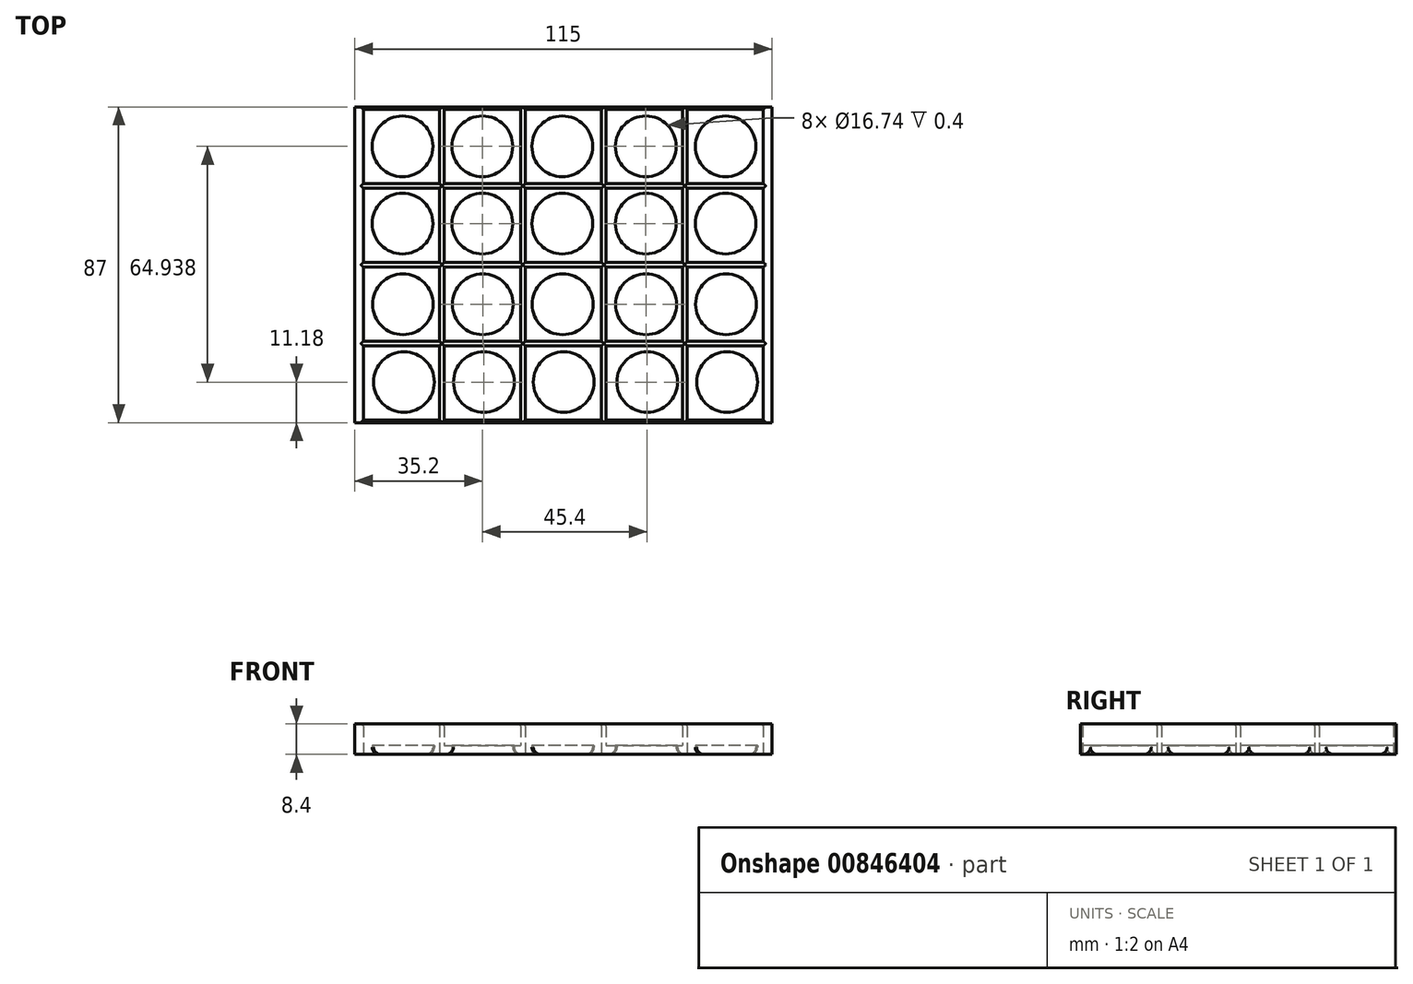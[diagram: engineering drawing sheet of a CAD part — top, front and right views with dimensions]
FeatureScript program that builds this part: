
annotation { "Feature Type Name" : "Feature", "Feature Type Description" : "" }
export const myFeature = defineFeature(function(context is Context, id is Id, definition is map)
    precondition{}
    {
        {
            var Q0;
            Q0=qCreatedBy(makeId("Top.planeOp"),FACE);
            var sketch = newSketch(context, id + "F0", { "sketchPlane" : qUnion([Q0])});
            skLineSegment(sketch, "E0.bottom", {"start": v(-57.5, 43.5) * mm, "end": v(57.5, 43.5) * mm});
            skLineSegment(sketch, "E0.top", {"start": v(-57.5, -43.5) * mm, "end": v(57.5, -43.5) * mm});
            skLineSegment(sketch, "E0.left", {"start": v(-57.5, 43.5) * mm, "end": v(-57.5, -43.5) * mm});
            skLineSegment(sketch, "E0.right", {"start": v(57.5, 43.5) * mm, "end": v(57.5, -43.5) * mm});
            skPoint(sketch, "E0.middle", {"position": v(0, 0) * mm});
            skCircle(sketch, "E1.MirrorC", {"center": v(-44.2, -10.9) * mm, "radius": 8.37 * mm});
            skCircle(sketch, "E2.MirrorC", {"center": v(-22.2, -10.9) * mm, "radius": 8.37 * mm});
            skCircle(sketch, "E3.MirrorC", {"center": v(-0.2, -10.9) * mm, "radius": 8.37 * mm});
            skCircle(sketch, "E4.MirrorC", {"center": v(22.8, -10.9) * mm, "radius": 8.37 * mm});
            skCircle(sketch, "E5.MirrorC", {"center": v(44.8, -10.9) * mm, "radius": 8.37 * mm});
            skLineSegment(sketch, "E6.0", {"start": v(-57.5, 42.8) * mm, "end": v(57.5, 42.8) * mm});
            skLineSegment(sketch, "E7.0", {"start": v(-57.5, -42.8) * mm, "end": v(57.5, -42.8) * mm});
            skLineSegment(sketch, "E8.0", {"start": v(-57.5, 22.32) * mm, "end": v(57.5, 22.32) * mm});
            skLineSegment(sketch, "E9.0", {"start": v(-57.5, -22.32) * mm, "end": v(57.5, -22.32) * mm});
            skLineSegment(sketch, "E10.0", {"start": v(-57.5, 21.12) * mm, "end": v(57.5, 21.12) * mm});
            skLineSegment(sketch, "E11.0", {"start": v(-57.5, -21.12) * mm, "end": v(57.5, -21.12) * mm});
            skLineSegment(sketch, "E12.0", {"start": v(-57.5, 0.64) * mm, "end": v(57.5, 0.64) * mm});
            skLineSegment(sketch, "E13.0", {"start": v(-57.5, -0.64) * mm, "end": v(57.5, -0.64) * mm});
            skLineSegment(sketch, "E14.0", {"start": v(55.1, 44.5) * mm, "end": v(55.1, -43.5) * mm});
            skLineSegment(sketch, "E15.0", {"start": v(34.1, 44.5) * mm, "end": v(34.1, -43.5) * mm});
            skLineSegment(sketch, "E16.0", {"start": v(32.8, 44.5) * mm, "end": v(32.8, -43.5) * mm});
            skLineSegment(sketch, "E17.0", {"start": v(11.8, 44.5) * mm, "end": v(11.8, -43.5) * mm});
            skLineSegment(sketch, "E18.0", {"start": v(10.5, 44.5) * mm, "end": v(10.5, -43.5) * mm});
            skLineSegment(sketch, "E19.0", {"start": v(-10.5, 44.5) * mm, "end": v(-10.5, -43.5) * mm});
            skLineSegment(sketch, "E20.0", {"start": v(-11.8, 44.5) * mm, "end": v(-11.8, -43.5) * mm});
            skLineSegment(sketch, "E21.0", {"start": v(-32.8, 44.5) * mm, "end": v(-32.8, -43.5) * mm});
            skLineSegment(sketch, "E22.0", {"start": v(-34.1, 44.5) * mm, "end": v(-34.1, -43.5) * mm});
            skLineSegment(sketch, "E23.0", {"start": v(-55.1, 44.5) * mm, "end": v(-55.1, -43.5) * mm});
            skCircle(sketch, "E24.MirrorC", {"center": v(-43.9, -32.32) * mm, "radius": 8.37 * mm});
            skCircle(sketch, "E25.MirrorC", {"center": v(-21.9, -32.32) * mm, "radius": 8.37 * mm});
            skCircle(sketch, "E26.MirrorC", {"center": v(0.1, -32.32) * mm, "radius": 8.37 * mm});
            skCircle(sketch, "E27.MirrorC", {"center": v(23.1, -32.32) * mm, "radius": 8.37 * mm});
            skCircle(sketch, "E28.MirrorC", {"center": v(45.1, -32.32) * mm, "radius": 8.37 * mm});
            skCircle(sketch, "E29.MirrorC", {"center": v(-44.3, 11.34) * mm, "radius": 8.37 * mm});
            skCircle(sketch, "E30.MirrorC", {"center": v(-22.3, 11.34) * mm, "radius": 8.37 * mm});
            skCircle(sketch, "E31.MirrorC", {"center": v(-0.3, 11.34) * mm, "radius": 8.37 * mm});
            skCircle(sketch, "E32.MirrorC", {"center": v(22.7, 11.34) * mm, "radius": 8.37 * mm});
            skCircle(sketch, "E33.MirrorC", {"center": v(44.7, 11.34) * mm, "radius": 8.37 * mm});
            skCircle(sketch, "E34.MirrorC", {"center": v(-44.3, 32.62) * mm, "radius": 8.37 * mm});
            skCircle(sketch, "E35.MirrorC", {"center": v(-22.3, 32.62) * mm, "radius": 8.37 * mm});
            skCircle(sketch, "E36.MirrorC", {"center": v(-0.3, 32.62) * mm, "radius": 8.37 * mm});
            skCircle(sketch, "E37.MirrorC", {"center": v(22.7, 32.62) * mm, "radius": 8.37 * mm});
            skCircle(sketch, "E38.MirrorC", {"center": v(44.7, 32.62) * mm, "radius": 8.37 * mm});
            skSolve(sketch);
        }
        {
            var Q0;
            {var subQ0=sQuery(id+"F0.wireOp",EDGE,"85c74178-88a3-4eaf-b492-32c6037f9e62.0");var subQ1=sQuery(id+"F0.wireOp",EDGE,"E0.left");var subQ2=makeQuery(id+"F0.imprint","INTERSECT",VERTEX,{"derivedFrom":[subQ1,subQ0]});Q0=makeQuery(id+"F0.imprint","IMPRINT",FACE,{"disambiguationData":[TD([[makeQuery(id+"F0.imprint","IMPRINT",EDGE,{"disambiguationData":[TD([[subQ2,-1.0]])],"derivedFrom":subQ1}),1.0]])]});}
            var Q1;
            {var subQ1=sQuery(id+"F0.wireOp",EDGE,"E0.bottom");var subQ6=sQuery(id+"F0.wireOp",EDGE,"E0.left");var subQ7=makeQuery(id+"F0.imprint","INTERSECT",VERTEX,{"derivedFrom":[subQ1,subQ6]});Q1=makeQuery(id+"F0.imprint","IMPRINT",FACE,{"disambiguationData":[TD([[makeQuery(id+"F0.imprint","IMPRINT",EDGE,{"disambiguationData":[TD([[subQ7,-1.0]])],"derivedFrom":subQ1}),-1.0]])]});}
            var Q2;
            {var subQ0=sQuery(id+"F0.wireOp",EDGE,"bdac1eed-a409-4cee-9b7b-61454a391d7d.0");var subQ1=sQuery(id+"F0.wireOp",EDGE,"E0.bottom");var subQ2=makeQuery(id+"F0.imprint","INTERSECT",VERTEX,{"derivedFrom":[subQ1,subQ0]});Q2=makeQuery(id+"F0.imprint","IMPRINT",FACE,{"disambiguationData":[TD([[makeQuery(id+"F0.imprint","IMPRINT",EDGE,{"disambiguationData":[TD([[subQ2,1.0]])],"derivedFrom":subQ1}),-1.0]])]});}
            var Q3;
            {var subQ0=sQuery(id+"F0.wireOp",EDGE,"23e37434-4ebb-4948-80c8-8d17bba51405.0");var subQ1=sQuery(id+"F0.wireOp",EDGE,"E0.bottom");var subQ2=makeQuery(id+"F0.imprint","INTERSECT",VERTEX,{"derivedFrom":[subQ1,subQ0]});Q3=makeQuery(id+"F0.imprint","IMPRINT",FACE,{"disambiguationData":[TD([[makeQuery(id+"F0.imprint","IMPRINT",EDGE,{"disambiguationData":[TD([[subQ2,1.0]])],"derivedFrom":subQ1}),-1.0]])]});}
            var Q4;
            {var subQ0=sQuery(id+"F0.wireOp",EDGE,"85c74178-88a3-4eaf-b492-32c6037f9e62.0");var subQ1=sQuery(id+"F0.wireOp",EDGE,"23e37434-4ebb-4948-80c8-8d17bba51405.0");var subQ2=makeQuery(id+"F0.imprint","INTERSECT",VERTEX,{"derivedFrom":[subQ1,subQ0]});Q4=makeQuery(id+"F0.imprint","IMPRINT",FACE,{"disambiguationData":[TD([[makeQuery(id+"F0.imprint","IMPRINT",EDGE,{"disambiguationData":[TD([[subQ2,-1.0]])],"derivedFrom":subQ1}),-1.0]])]});}
            var Q5;
            {var subQ0=sQuery(id+"F0.wireOp",EDGE,"f9003588-73a7-42be-b55c-edd191297de8.0");var subQ1=sQuery(id+"F0.wireOp",EDGE,"E0.bottom");var subQ2=makeQuery(id+"F0.imprint","INTERSECT",VERTEX,{"derivedFrom":[subQ1,subQ0]});Q5=makeQuery(id+"F0.imprint","IMPRINT",FACE,{"disambiguationData":[TD([[makeQuery(id+"F0.imprint","IMPRINT",EDGE,{"disambiguationData":[TD([[subQ2,1.0]])],"derivedFrom":subQ1}),-1.0]])]});}
            var Q6;
            {var subQ0=sQuery(id+"F0.wireOp",EDGE,"a62689d6-4df4-411d-a8de-d30e4e7abbb4.0");var subQ1=sQuery(id+"F0.wireOp",EDGE,"E0.bottom");var subQ2=makeQuery(id+"F0.imprint","INTERSECT",VERTEX,{"derivedFrom":[subQ1,subQ0]});Q6=makeQuery(id+"F0.imprint","IMPRINT",FACE,{"disambiguationData":[TD([[makeQuery(id+"F0.imprint","IMPRINT",EDGE,{"disambiguationData":[TD([[subQ2,1.0]])],"derivedFrom":subQ1}),-1.0]])]});}
            var Q7;
            {var subQ0=sQuery(id+"F0.wireOp",EDGE,"989afcd3-5a0d-4914-9734-28e95c678f40.0");var subQ1=sQuery(id+"F0.wireOp",EDGE,"E0.bottom");var subQ2=makeQuery(id+"F0.imprint","INTERSECT",VERTEX,{"derivedFrom":[subQ1,subQ0]});Q7=makeQuery(id+"F0.imprint","IMPRINT",FACE,{"disambiguationData":[TD([[makeQuery(id+"F0.imprint","IMPRINT",EDGE,{"disambiguationData":[TD([[subQ2,1.0]])],"derivedFrom":subQ1}),-1.0]])]});}
            var Q8;
            {var subQ0=sQuery(id+"F0.wireOp",EDGE,"862523a1-1db9-4ec9-a786-b55df2c1a98e.0");var subQ1=sQuery(id+"F0.wireOp",EDGE,"E0.bottom");var subQ2=makeQuery(id+"F0.imprint","INTERSECT",VERTEX,{"derivedFrom":[subQ1,subQ0]});Q8=makeQuery(id+"F0.imprint","IMPRINT",FACE,{"disambiguationData":[TD([[makeQuery(id+"F0.imprint","IMPRINT",EDGE,{"disambiguationData":[TD([[subQ2,1.0]])],"derivedFrom":subQ1}),-1.0]])]});}
            var Q9;
            {var subQ0=sQuery(id+"F0.wireOp",EDGE,"E0.right");var subQ1=sQuery(id+"F0.wireOp",EDGE,"E0.bottom");var subQ2=makeQuery(id+"F0.imprint","INTERSECT",VERTEX,{"derivedFrom":[subQ1,subQ0]});Q9=makeQuery(id+"F0.imprint","IMPRINT",FACE,{"disambiguationData":[TD([[makeQuery(id+"F0.imprint","IMPRINT",EDGE,{"disambiguationData":[TD([[subQ2,1.0]])],"derivedFrom":subQ1}),-1.0]])]});}
            var Q10;
            {var subQ0=sQuery(id+"F0.wireOp",EDGE,"85c74178-88a3-4eaf-b492-32c6037f9e62.0");var subQ1=sQuery(id+"F0.wireOp",EDGE,"E0.right");var subQ2=makeQuery(id+"F0.imprint","INTERSECT",VERTEX,{"derivedFrom":[subQ1,subQ0]});Q10=makeQuery(id+"F0.imprint","IMPRINT",FACE,{"disambiguationData":[TD([[makeQuery(id+"F0.imprint","IMPRINT",EDGE,{"disambiguationData":[TD([[subQ2,-1.0]])],"derivedFrom":subQ1}),-1.0]])]});}
            var Q11;
            {var subQ0=sQuery(id+"F0.wireOp",EDGE,"919ec9c0-a23d-4d93-b64b-cbbe13223f10.0");var subQ1=sQuery(id+"F0.wireOp",EDGE,"E0.right");var subQ2=makeQuery(id+"F0.imprint","INTERSECT",VERTEX,{"derivedFrom":[subQ1,subQ0]});Q11=makeQuery(id+"F0.imprint","IMPRINT",FACE,{"disambiguationData":[TD([[makeQuery(id+"F0.imprint","IMPRINT",EDGE,{"disambiguationData":[TD([[subQ2,-1.0]])],"derivedFrom":subQ1}),-1.0]])]});}
            var Q12;
            {var subQ0=sQuery(id+"F0.wireOp",EDGE,"919ec9c0-a23d-4d93-b64b-cbbe13223f10.0");var subQ1=sQuery(id+"F0.wireOp",EDGE,"862523a1-1db9-4ec9-a786-b55df2c1a98e.0");var subQ2=makeQuery(id+"F0.imprint","INTERSECT",VERTEX,{"derivedFrom":[subQ1,subQ0]});Q12=makeQuery(id+"F0.imprint","IMPRINT",FACE,{"disambiguationData":[TD([[makeQuery(id+"F0.imprint","IMPRINT",EDGE,{"disambiguationData":[TD([[subQ2,-1.0]])],"derivedFrom":subQ1}),-1.0]])]});}
            var Q13;
            {var subQ0=sQuery(id+"F0.wireOp",EDGE,"919ec9c0-a23d-4d93-b64b-cbbe13223f10.0");var subQ1=sQuery(id+"F0.wireOp",EDGE,"989afcd3-5a0d-4914-9734-28e95c678f40.0");var subQ2=makeQuery(id+"F0.imprint","INTERSECT",VERTEX,{"derivedFrom":[subQ1,subQ0]});Q13=makeQuery(id+"F0.imprint","IMPRINT",FACE,{"disambiguationData":[TD([[makeQuery(id+"F0.imprint","IMPRINT",EDGE,{"disambiguationData":[TD([[subQ2,-1.0]])],"derivedFrom":subQ1}),-1.0]])]});}
            var Q14;
            {var subQ0=sQuery(id+"F0.wireOp",EDGE,"85c74178-88a3-4eaf-b492-32c6037f9e62.0");var subQ1=sQuery(id+"F0.wireOp",EDGE,"989afcd3-5a0d-4914-9734-28e95c678f40.0");var subQ2=makeQuery(id+"F0.imprint","INTERSECT",VERTEX,{"derivedFrom":[subQ1,subQ0]});Q14=makeQuery(id+"F0.imprint","IMPRINT",FACE,{"disambiguationData":[TD([[makeQuery(id+"F0.imprint","IMPRINT",EDGE,{"disambiguationData":[TD([[subQ2,-1.0]])],"derivedFrom":subQ1}),-1.0]])]});}
            var Q15;
            {var subQ0=sQuery(id+"F0.wireOp",EDGE,"450db5bc-e2e3-4f88-b9d5-953014a2ba1e.0");var subQ1=sQuery(id+"F0.wireOp",EDGE,"989afcd3-5a0d-4914-9734-28e95c678f40.0");var subQ2=makeQuery(id+"F0.imprint","INTERSECT",VERTEX,{"derivedFrom":[subQ1,subQ0]});Q15=makeQuery(id+"F0.imprint","IMPRINT",FACE,{"disambiguationData":[TD([[makeQuery(id+"F0.imprint","IMPRINT",EDGE,{"disambiguationData":[TD([[subQ2,-1.0]])],"derivedFrom":subQ1}),-1.0]])]});}
            var Q16;
            {var subQ0=sQuery(id+"F0.wireOp",EDGE,"450db5bc-e2e3-4f88-b9d5-953014a2ba1e.0");var subQ1=sQuery(id+"F0.wireOp",EDGE,"E0.right");var subQ2=makeQuery(id+"F0.imprint","INTERSECT",VERTEX,{"derivedFrom":[subQ1,subQ0]});Q16=makeQuery(id+"F0.imprint","IMPRINT",FACE,{"disambiguationData":[TD([[makeQuery(id+"F0.imprint","IMPRINT",EDGE,{"disambiguationData":[TD([[subQ2,-1.0]])],"derivedFrom":subQ1}),-1.0]])]});}
            var Q17;
            {var subQ0=sQuery(id+"F0.wireOp",EDGE,"681770c7-baf9-4a3d-b09d-7c4e2b6cc42b.0");var subQ1=sQuery(id+"F0.wireOp",EDGE,"E0.right");var subQ2=makeQuery(id+"F0.imprint","INTERSECT",VERTEX,{"derivedFrom":[subQ1,subQ0]});Q17=makeQuery(id+"F0.imprint","IMPRINT",FACE,{"disambiguationData":[TD([[makeQuery(id+"F0.imprint","IMPRINT",EDGE,{"disambiguationData":[TD([[subQ2,-1.0]])],"derivedFrom":subQ1}),-1.0]])]});}
            var Q18;
            {var subQ0=sQuery(id+"F0.wireOp",EDGE,"a21ffa6c-e3b5-4756-9eef-63544e5bc852.0");var subQ1=sQuery(id+"F0.wireOp",EDGE,"E0.right");var subQ2=makeQuery(id+"F0.imprint","INTERSECT",VERTEX,{"derivedFrom":[subQ1,subQ0]});Q18=makeQuery(id+"F0.imprint","IMPRINT",FACE,{"disambiguationData":[TD([[makeQuery(id+"F0.imprint","IMPRINT",EDGE,{"disambiguationData":[TD([[subQ2,-1.0]])],"derivedFrom":subQ1}),-1.0]])]});}
            var Q19;
            {var subQ0=sQuery(id+"F0.wireOp",EDGE,"a21ffa6c-e3b5-4756-9eef-63544e5bc852.0");var subQ1=sQuery(id+"F0.wireOp",EDGE,"989afcd3-5a0d-4914-9734-28e95c678f40.0");var subQ2=makeQuery(id+"F0.imprint","INTERSECT",VERTEX,{"derivedFrom":[subQ1,subQ0]});Q19=makeQuery(id+"F0.imprint","IMPRINT",FACE,{"disambiguationData":[TD([[makeQuery(id+"F0.imprint","IMPRINT",EDGE,{"disambiguationData":[TD([[subQ2,-1.0]])],"derivedFrom":subQ1}),-1.0]])]});}
            var Q20;
            {var subQ0=sQuery(id+"F0.wireOp",EDGE,"681770c7-baf9-4a3d-b09d-7c4e2b6cc42b.0");var subQ1=sQuery(id+"F0.wireOp",EDGE,"989afcd3-5a0d-4914-9734-28e95c678f40.0");var subQ2=makeQuery(id+"F0.imprint","INTERSECT",VERTEX,{"derivedFrom":[subQ1,subQ0]});Q20=makeQuery(id+"F0.imprint","IMPRINT",FACE,{"disambiguationData":[TD([[makeQuery(id+"F0.imprint","IMPRINT",EDGE,{"disambiguationData":[TD([[subQ2,-1.0]])],"derivedFrom":subQ1}),-1.0]])]});}
            var Q21;
            {var subQ0=sQuery(id+"F0.wireOp",EDGE,"0a55f61a-76dd-4ac3-9223-154b0b1f7dfb.0");var subQ1=sQuery(id+"F0.wireOp",EDGE,"989afcd3-5a0d-4914-9734-28e95c678f40.0");var subQ2=makeQuery(id+"F0.imprint","INTERSECT",VERTEX,{"derivedFrom":[subQ1,subQ0]});Q21=makeQuery(id+"F0.imprint","IMPRINT",FACE,{"disambiguationData":[TD([[makeQuery(id+"F0.imprint","IMPRINT",EDGE,{"disambiguationData":[TD([[subQ2,-1.0]])],"derivedFrom":subQ1}),-1.0]])]});}
            var Q22;
            {var subQ0=sQuery(id+"F0.wireOp",EDGE,"854f07df-45a9-419d-971c-554534df12f4.0");var subQ1=sQuery(id+"F0.wireOp",EDGE,"989afcd3-5a0d-4914-9734-28e95c678f40.0");var subQ2=makeQuery(id+"F0.imprint","INTERSECT",VERTEX,{"derivedFrom":[subQ1,subQ0]});Q22=makeQuery(id+"F0.imprint","IMPRINT",FACE,{"disambiguationData":[TD([[makeQuery(id+"F0.imprint","IMPRINT",EDGE,{"disambiguationData":[TD([[subQ2,1.0]])],"derivedFrom":subQ1}),-1.0]])]});}
            var Q23;
            {var subQ0=sQuery(id+"F0.wireOp",EDGE,"0c15ec7b-9e92-4eb4-8615-29722b4b26f3.0");var subQ1=sQuery(id+"F0.wireOp",EDGE,"E0.right");var subQ2=makeQuery(id+"F0.imprint","INTERSECT",VERTEX,{"derivedFrom":[subQ1,subQ0]});Q23=makeQuery(id+"F0.imprint","IMPRINT",FACE,{"disambiguationData":[TD([[makeQuery(id+"F0.imprint","IMPRINT",EDGE,{"disambiguationData":[TD([[subQ2,-1.0]])],"derivedFrom":subQ1}),-1.0]])]});}
            var Q24;
            {var subQ0=sQuery(id+"F0.wireOp",EDGE,"0a55f61a-76dd-4ac3-9223-154b0b1f7dfb.0");var subQ1=sQuery(id+"F0.wireOp",EDGE,"862523a1-1db9-4ec9-a786-b55df2c1a98e.0");var subQ2=makeQuery(id+"F0.imprint","INTERSECT",VERTEX,{"derivedFrom":[subQ1,subQ0]});Q24=makeQuery(id+"F0.imprint","IMPRINT",FACE,{"disambiguationData":[TD([[makeQuery(id+"F0.imprint","IMPRINT",EDGE,{"disambiguationData":[TD([[subQ2,-1.0]])],"derivedFrom":subQ1}),-1.0]])]});}
            var Q25;
            {var subQ4=sQuery(id+"F0.wireOp",EDGE,"E0.right");var subQ5=sQuery(id+"F0.wireOp",EDGE,"E0.top");var subQ6=makeQuery(id+"F0.imprint","INTERSECT",VERTEX,{"derivedFrom":[subQ5,subQ4]});Q25=makeQuery(id+"F0.imprint","IMPRINT",FACE,{"disambiguationData":[TD([[makeQuery(id+"F0.imprint","IMPRINT",EDGE,{"disambiguationData":[TD([[subQ6,1.0]])],"derivedFrom":subQ5}),1.0]])]});}
            var Q26;
            {var subQ0=sQuery(id+"F0.wireOp",EDGE,"3e5cf576-49dc-4465-ad3e-ca1242db3cf5.0");var subQ1=sQuery(id+"F0.wireOp",EDGE,"E0.top");var subQ2=makeQuery(id+"F0.imprint","INTERSECT",VERTEX,{"derivedFrom":[subQ1,subQ0]});Q26=makeQuery(id+"F0.imprint","IMPRINT",FACE,{"disambiguationData":[TD([[makeQuery(id+"F0.imprint","IMPRINT",EDGE,{"disambiguationData":[TD([[subQ2,-1.0]])],"derivedFrom":subQ1}),1.0]])]});}
            var Q27;
            {var subQ0=sQuery(id+"F0.wireOp",EDGE,"E0.left");var subQ1=sQuery(id+"F0.wireOp",EDGE,"E0.top");var subQ2=makeQuery(id+"F0.imprint","INTERSECT",VERTEX,{"derivedFrom":[subQ1,subQ0]});Q27=makeQuery(id+"F0.imprint","IMPRINT",FACE,{"disambiguationData":[TD([[makeQuery(id+"F0.imprint","IMPRINT",EDGE,{"disambiguationData":[TD([[subQ2,-1.0]])],"derivedFrom":subQ1}),1.0]])]});}
            var Q28;
            {var subQ0=sQuery(id+"F0.wireOp",EDGE,"b2fe94c1-cc08-47c4-b663-ca396442125b.0");var subQ1=sQuery(id+"F0.wireOp",EDGE,"E0.top");var subQ2=makeQuery(id+"F0.imprint","INTERSECT",VERTEX,{"derivedFrom":[subQ1,subQ0]});Q28=makeQuery(id+"F0.imprint","IMPRINT",FACE,{"disambiguationData":[TD([[makeQuery(id+"F0.imprint","IMPRINT",EDGE,{"disambiguationData":[TD([[subQ2,-1.0]])],"derivedFrom":subQ1}),1.0]])]});}
            var Q29;
            {var subQ0=sQuery(id+"F0.wireOp",EDGE,"0c15ec7b-9e92-4eb4-8615-29722b4b26f3.0");var subQ1=sQuery(id+"F0.wireOp",EDGE,"b2fe94c1-cc08-47c4-b663-ca396442125b.0");var subQ2=makeQuery(id+"F0.imprint","INTERSECT",VERTEX,{"derivedFrom":[subQ1,subQ0]});Q29=makeQuery(id+"F0.imprint","IMPRINT",FACE,{"disambiguationData":[TD([[makeQuery(id+"F0.imprint","IMPRINT",EDGE,{"disambiguationData":[TD([[subQ2,-1.0]])],"derivedFrom":subQ1}),1.0]])]});}
            var Q30;
            {var subQ0=sQuery(id+"F0.wireOp",EDGE,"0a55f61a-76dd-4ac3-9223-154b0b1f7dfb.0");var subQ1=sQuery(id+"F0.wireOp",EDGE,"b2fe94c1-cc08-47c4-b663-ca396442125b.0");var subQ2=makeQuery(id+"F0.imprint","INTERSECT",VERTEX,{"derivedFrom":[subQ1,subQ0]});Q30=makeQuery(id+"F0.imprint","IMPRINT",FACE,{"disambiguationData":[TD([[makeQuery(id+"F0.imprint","IMPRINT",EDGE,{"disambiguationData":[TD([[subQ2,-1.0]])],"derivedFrom":subQ1}),1.0]])]});}
            var Q31;
            {var subQ0=sQuery(id+"F0.wireOp",EDGE,"0a55f61a-76dd-4ac3-9223-154b0b1f7dfb.0");var subQ1=sQuery(id+"F0.wireOp",EDGE,"3e5cf576-49dc-4465-ad3e-ca1242db3cf5.0");var subQ2=makeQuery(id+"F0.imprint","INTERSECT",VERTEX,{"derivedFrom":[subQ1,subQ0]});Q31=makeQuery(id+"F0.imprint","IMPRINT",FACE,{"disambiguationData":[TD([[makeQuery(id+"F0.imprint","IMPRINT",EDGE,{"disambiguationData":[TD([[subQ2,-1.0]])],"derivedFrom":subQ1}),1.0]])]});}
            var Q32;
            {var subQ0=sQuery(id+"F0.wireOp",EDGE,"0c15ec7b-9e92-4eb4-8615-29722b4b26f3.0");var subQ1=sQuery(id+"F0.wireOp",EDGE,"E0.left");var subQ2=makeQuery(id+"F0.imprint","INTERSECT",VERTEX,{"derivedFrom":[subQ1,subQ0]});Q32=makeQuery(id+"F0.imprint","IMPRINT",FACE,{"disambiguationData":[TD([[makeQuery(id+"F0.imprint","IMPRINT",EDGE,{"disambiguationData":[TD([[subQ2,-1.0]])],"derivedFrom":subQ1}),1.0]])]});}
            var Q33;
            {var subQ0=sQuery(id+"F0.wireOp",EDGE,"0a55f61a-76dd-4ac3-9223-154b0b1f7dfb.0");var subQ1=sQuery(id+"F0.wireOp",EDGE,"E0.left");var subQ2=makeQuery(id+"F0.imprint","INTERSECT",VERTEX,{"derivedFrom":[subQ1,subQ0]});Q33=makeQuery(id+"F0.imprint","IMPRINT",FACE,{"disambiguationData":[TD([[makeQuery(id+"F0.imprint","IMPRINT",EDGE,{"disambiguationData":[TD([[subQ2,-1.0]])],"derivedFrom":subQ1}),1.0]])]});}
            var Q34;
            {var subQ0=sQuery(id+"F0.wireOp",EDGE,"681770c7-baf9-4a3d-b09d-7c4e2b6cc42b.0");var subQ1=sQuery(id+"F0.wireOp",EDGE,"E0.left");var subQ2=makeQuery(id+"F0.imprint","INTERSECT",VERTEX,{"derivedFrom":[subQ1,subQ0]});Q34=makeQuery(id+"F0.imprint","IMPRINT",FACE,{"disambiguationData":[TD([[makeQuery(id+"F0.imprint","IMPRINT",EDGE,{"disambiguationData":[TD([[subQ2,-1.0]])],"derivedFrom":subQ1}),1.0]])]});}
            var Q35;
            {var subQ0=sQuery(id+"F0.wireOp",EDGE,"a21ffa6c-e3b5-4756-9eef-63544e5bc852.0");var subQ1=sQuery(id+"F0.wireOp",EDGE,"E0.left");var subQ2=makeQuery(id+"F0.imprint","INTERSECT",VERTEX,{"derivedFrom":[subQ1,subQ0]});Q35=makeQuery(id+"F0.imprint","IMPRINT",FACE,{"disambiguationData":[TD([[makeQuery(id+"F0.imprint","IMPRINT",EDGE,{"disambiguationData":[TD([[subQ2,-1.0]])],"derivedFrom":subQ1}),1.0]])]});}
            var Q36;
            {var subQ0=sQuery(id+"F0.wireOp",EDGE,"450db5bc-e2e3-4f88-b9d5-953014a2ba1e.0");var subQ1=sQuery(id+"F0.wireOp",EDGE,"E0.left");var subQ2=makeQuery(id+"F0.imprint","INTERSECT",VERTEX,{"derivedFrom":[subQ1,subQ0]});Q36=makeQuery(id+"F0.imprint","IMPRINT",FACE,{"disambiguationData":[TD([[makeQuery(id+"F0.imprint","IMPRINT",EDGE,{"disambiguationData":[TD([[subQ2,-1.0]])],"derivedFrom":subQ1}),1.0]])]});}
            var Q37;
            {var subQ0=sQuery(id+"F0.wireOp",EDGE,"919ec9c0-a23d-4d93-b64b-cbbe13223f10.0");var subQ1=sQuery(id+"F0.wireOp",EDGE,"E0.left");var subQ2=makeQuery(id+"F0.imprint","INTERSECT",VERTEX,{"derivedFrom":[subQ1,subQ0]});Q37=makeQuery(id+"F0.imprint","IMPRINT",FACE,{"disambiguationData":[TD([[makeQuery(id+"F0.imprint","IMPRINT",EDGE,{"disambiguationData":[TD([[subQ2,-1.0]])],"derivedFrom":subQ1}),1.0]])]});}
            var Q38;
            {var subQ0=sQuery(id+"F0.wireOp",EDGE,"919ec9c0-a23d-4d93-b64b-cbbe13223f10.0");var subQ1=sQuery(id+"F0.wireOp",EDGE,"3e5cf576-49dc-4465-ad3e-ca1242db3cf5.0");var subQ2=makeQuery(id+"F0.imprint","INTERSECT",VERTEX,{"derivedFrom":[subQ1,subQ0]});Q38=makeQuery(id+"F0.imprint","IMPRINT",FACE,{"disambiguationData":[TD([[makeQuery(id+"F0.imprint","IMPRINT",EDGE,{"disambiguationData":[TD([[subQ2,-1.0]])],"derivedFrom":subQ1}),1.0]])]});}
            var Q39;
            {var subQ0=sQuery(id+"F0.wireOp",EDGE,"919ec9c0-a23d-4d93-b64b-cbbe13223f10.0");var subQ1=sQuery(id+"F0.wireOp",EDGE,"b2fe94c1-cc08-47c4-b663-ca396442125b.0");var subQ2=makeQuery(id+"F0.imprint","INTERSECT",VERTEX,{"derivedFrom":[subQ1,subQ0]});Q39=makeQuery(id+"F0.imprint","IMPRINT",FACE,{"disambiguationData":[TD([[makeQuery(id+"F0.imprint","IMPRINT",EDGE,{"disambiguationData":[TD([[subQ2,-1.0]])],"derivedFrom":subQ1}),1.0]])]});}
            var Q40;
            {var subQ0=sQuery(id+"F0.wireOp",EDGE,"85c74178-88a3-4eaf-b492-32c6037f9e62.0");var subQ1=sQuery(id+"F0.wireOp",EDGE,"b2fe94c1-cc08-47c4-b663-ca396442125b.0");var subQ2=makeQuery(id+"F0.imprint","INTERSECT",VERTEX,{"derivedFrom":[subQ1,subQ0]});Q40=makeQuery(id+"F0.imprint","IMPRINT",FACE,{"disambiguationData":[TD([[makeQuery(id+"F0.imprint","IMPRINT",EDGE,{"disambiguationData":[TD([[subQ2,-1.0]])],"derivedFrom":subQ1}),1.0]])]});}
            var Q41;
            {var subQ0=sQuery(id+"F0.wireOp",EDGE,"a21ffa6c-e3b5-4756-9eef-63544e5bc852.0");var subQ1=sQuery(id+"F0.wireOp",EDGE,"3e5cf576-49dc-4465-ad3e-ca1242db3cf5.0");var subQ2=makeQuery(id+"F0.imprint","INTERSECT",VERTEX,{"derivedFrom":[subQ1,subQ0]});Q41=makeQuery(id+"F0.imprint","IMPRINT",FACE,{"disambiguationData":[TD([[makeQuery(id+"F0.imprint","IMPRINT",EDGE,{"disambiguationData":[TD([[subQ2,-1.0]])],"derivedFrom":subQ1}),1.0]])]});}
            var Q42;
            {var subQ0=sQuery(id+"F0.wireOp",EDGE,"a21ffa6c-e3b5-4756-9eef-63544e5bc852.0");var subQ1=sQuery(id+"F0.wireOp",EDGE,"9343b0c3-cd2f-487d-bd13-aee8d7f259e0.0");var subQ2=makeQuery(id+"F0.imprint","INTERSECT",VERTEX,{"derivedFrom":[subQ1,subQ0]});Q42=makeQuery(id+"F0.imprint","IMPRINT",FACE,{"disambiguationData":[TD([[makeQuery(id+"F0.imprint","IMPRINT",EDGE,{"disambiguationData":[TD([[subQ2,-1.0]])],"derivedFrom":subQ1}),1.0]])]});}
            var Q43;
            {var subQ0=sQuery(id+"F0.wireOp",EDGE,"919ec9c0-a23d-4d93-b64b-cbbe13223f10.0");var subQ1=sQuery(id+"F0.wireOp",EDGE,"9343b0c3-cd2f-487d-bd13-aee8d7f259e0.0");var subQ2=makeQuery(id+"F0.imprint","INTERSECT",VERTEX,{"derivedFrom":[subQ1,subQ0]});Q43=makeQuery(id+"F0.imprint","IMPRINT",FACE,{"disambiguationData":[TD([[makeQuery(id+"F0.imprint","IMPRINT",EDGE,{"disambiguationData":[TD([[subQ2,-1.0]])],"derivedFrom":subQ1}),1.0]])]});}
            var Q44;
            {var subQ0=sQuery(id+"F0.wireOp",EDGE,"919ec9c0-a23d-4d93-b64b-cbbe13223f10.0");var subQ1=sQuery(id+"F0.wireOp",EDGE,"23e37434-4ebb-4948-80c8-8d17bba51405.0");var subQ2=makeQuery(id+"F0.imprint","INTERSECT",VERTEX,{"derivedFrom":[subQ1,subQ0]});Q44=makeQuery(id+"F0.imprint","IMPRINT",FACE,{"disambiguationData":[TD([[makeQuery(id+"F0.imprint","IMPRINT",EDGE,{"disambiguationData":[TD([[subQ2,-1.0]])],"derivedFrom":subQ1}),-1.0]])]});}
            var Q45;
            {var subQ0=sQuery(id+"F0.wireOp",EDGE,"450db5bc-e2e3-4f88-b9d5-953014a2ba1e.0");var subQ1=sQuery(id+"F0.wireOp",EDGE,"23e37434-4ebb-4948-80c8-8d17bba51405.0");var subQ2=makeQuery(id+"F0.imprint","INTERSECT",VERTEX,{"derivedFrom":[subQ1,subQ0]});Q45=makeQuery(id+"F0.imprint","IMPRINT",FACE,{"disambiguationData":[TD([[makeQuery(id+"F0.imprint","IMPRINT",EDGE,{"disambiguationData":[TD([[subQ2,-1.0]])],"derivedFrom":subQ1}),-1.0]])]});}
            var Q46;
            {var subQ0=sQuery(id+"F0.wireOp",EDGE,"919ec9c0-a23d-4d93-b64b-cbbe13223f10.0");var subQ1=sQuery(id+"F0.wireOp",EDGE,"bdac1eed-a409-4cee-9b7b-61454a391d7d.0");var subQ2=makeQuery(id+"F0.imprint","INTERSECT",VERTEX,{"derivedFrom":[subQ1,subQ0]});Q46=makeQuery(id+"F0.imprint","IMPRINT",FACE,{"disambiguationData":[TD([[makeQuery(id+"F0.imprint","IMPRINT",EDGE,{"disambiguationData":[TD([[subQ2,-1.0]])],"derivedFrom":subQ1}),-1.0]])]});}
            var Q47;
            {var subQ0=sQuery(id+"F0.wireOp",EDGE,"85c74178-88a3-4eaf-b492-32c6037f9e62.0");var subQ1=sQuery(id+"F0.wireOp",EDGE,"f9003588-73a7-42be-b55c-edd191297de8.0");var subQ2=makeQuery(id+"F0.imprint","INTERSECT",VERTEX,{"derivedFrom":[subQ1,subQ0]});Q47=makeQuery(id+"F0.imprint","IMPRINT",FACE,{"disambiguationData":[TD([[makeQuery(id+"F0.imprint","IMPRINT",EDGE,{"disambiguationData":[TD([[subQ2,-1.0]])],"derivedFrom":subQ1}),-1.0]])]});}
            var Q48;
            {var subQ0=sQuery(id+"F0.wireOp",EDGE,"919ec9c0-a23d-4d93-b64b-cbbe13223f10.0");var subQ1=sQuery(id+"F0.wireOp",EDGE,"f9003588-73a7-42be-b55c-edd191297de8.0");var subQ2=makeQuery(id+"F0.imprint","INTERSECT",VERTEX,{"derivedFrom":[subQ1,subQ0]});Q48=makeQuery(id+"F0.imprint","IMPRINT",FACE,{"disambiguationData":[TD([[makeQuery(id+"F0.imprint","IMPRINT",EDGE,{"disambiguationData":[TD([[subQ2,-1.0]])],"derivedFrom":subQ1}),-1.0]])]});}
            var Q49;
            {var subQ0=sQuery(id+"F0.wireOp",EDGE,"919ec9c0-a23d-4d93-b64b-cbbe13223f10.0");var subQ1=sQuery(id+"F0.wireOp",EDGE,"a62689d6-4df4-411d-a8de-d30e4e7abbb4.0");var subQ2=makeQuery(id+"F0.imprint","INTERSECT",VERTEX,{"derivedFrom":[subQ1,subQ0]});Q49=makeQuery(id+"F0.imprint","IMPRINT",FACE,{"disambiguationData":[TD([[makeQuery(id+"F0.imprint","IMPRINT",EDGE,{"disambiguationData":[TD([[subQ2,-1.0]])],"derivedFrom":subQ1}),-1.0]])]});}
            var Q50;
            {var subQ0=sQuery(id+"F0.wireOp",EDGE,"a21ffa6c-e3b5-4756-9eef-63544e5bc852.0");var subQ1=sQuery(id+"F0.wireOp",EDGE,"f9003588-73a7-42be-b55c-edd191297de8.0");var subQ2=makeQuery(id+"F0.imprint","INTERSECT",VERTEX,{"derivedFrom":[subQ1,subQ0]});Q50=makeQuery(id+"F0.imprint","IMPRINT",FACE,{"disambiguationData":[TD([[makeQuery(id+"F0.imprint","IMPRINT",EDGE,{"disambiguationData":[TD([[subQ2,-1.0]])],"derivedFrom":subQ1}),-1.0]])]});}
            var Q51;
            {var subQ0=sQuery(id+"F0.wireOp",EDGE,"a21ffa6c-e3b5-4756-9eef-63544e5bc852.0");var subQ1=sQuery(id+"F0.wireOp",EDGE,"23e37434-4ebb-4948-80c8-8d17bba51405.0");var subQ2=makeQuery(id+"F0.imprint","INTERSECT",VERTEX,{"derivedFrom":[subQ1,subQ0]});Q51=makeQuery(id+"F0.imprint","IMPRINT",FACE,{"disambiguationData":[TD([[makeQuery(id+"F0.imprint","IMPRINT",EDGE,{"disambiguationData":[TD([[subQ2,-1.0]])],"derivedFrom":subQ1}),-1.0]])]});}
            var Q52;
            {var subQ0=sQuery(id+"F0.wireOp",EDGE,"a21ffa6c-e3b5-4756-9eef-63544e5bc852.0");var subQ1=sQuery(id+"F0.wireOp",EDGE,"b2fe94c1-cc08-47c4-b663-ca396442125b.0");var subQ2=makeQuery(id+"F0.imprint","INTERSECT",VERTEX,{"derivedFrom":[subQ1,subQ0]});Q52=makeQuery(id+"F0.imprint","IMPRINT",FACE,{"disambiguationData":[TD([[makeQuery(id+"F0.imprint","IMPRINT",EDGE,{"disambiguationData":[TD([[subQ2,-1.0]])],"derivedFrom":subQ1}),1.0]])]});}
            var Q53;
            {var subQ0=sQuery(id+"F0.wireOp",EDGE,"681770c7-baf9-4a3d-b09d-7c4e2b6cc42b.0");var subQ1=sQuery(id+"F0.wireOp",EDGE,"23e37434-4ebb-4948-80c8-8d17bba51405.0");var subQ2=makeQuery(id+"F0.imprint","INTERSECT",VERTEX,{"derivedFrom":[subQ1,subQ0]});Q53=makeQuery(id+"F0.imprint","IMPRINT",FACE,{"disambiguationData":[TD([[makeQuery(id+"F0.imprint","IMPRINT",EDGE,{"disambiguationData":[TD([[subQ2,-1.0]])],"derivedFrom":subQ1}),-1.0]])]});}
            var Q54;
            {var subQ0=sQuery(id+"F0.wireOp",EDGE,"681770c7-baf9-4a3d-b09d-7c4e2b6cc42b.0");var subQ1=sQuery(id+"F0.wireOp",EDGE,"b2fe94c1-cc08-47c4-b663-ca396442125b.0");var subQ2=makeQuery(id+"F0.imprint","INTERSECT",VERTEX,{"derivedFrom":[subQ1,subQ0]});Q54=makeQuery(id+"F0.imprint","IMPRINT",FACE,{"disambiguationData":[TD([[makeQuery(id+"F0.imprint","IMPRINT",EDGE,{"disambiguationData":[TD([[subQ2,-1.0]])],"derivedFrom":subQ1}),1.0]])]});}
            var Q55;
            {var subQ0=sQuery(id+"F0.wireOp",EDGE,"450db5bc-e2e3-4f88-b9d5-953014a2ba1e.0");var subQ1=sQuery(id+"F0.wireOp",EDGE,"b2fe94c1-cc08-47c4-b663-ca396442125b.0");var subQ2=makeQuery(id+"F0.imprint","INTERSECT",VERTEX,{"derivedFrom":[subQ1,subQ0]});Q55=makeQuery(id+"F0.imprint","IMPRINT",FACE,{"disambiguationData":[TD([[makeQuery(id+"F0.imprint","IMPRINT",EDGE,{"disambiguationData":[TD([[subQ2,-1.0]])],"derivedFrom":subQ1}),1.0]])]});}
            var Q56;
            {var subQ0=sQuery(id+"F0.wireOp",EDGE,"0a55f61a-76dd-4ac3-9223-154b0b1f7dfb.0");var subQ1=sQuery(id+"F0.wireOp",EDGE,"23e37434-4ebb-4948-80c8-8d17bba51405.0");var subQ2=makeQuery(id+"F0.imprint","INTERSECT",VERTEX,{"derivedFrom":[subQ1,subQ0]});Q56=makeQuery(id+"F0.imprint","IMPRINT",FACE,{"disambiguationData":[TD([[makeQuery(id+"F0.imprint","IMPRINT",EDGE,{"disambiguationData":[TD([[subQ2,-1.0]])],"derivedFrom":subQ1}),-1.0]])]});}
            var Q57;
            {var subQ0=sQuery(id+"F0.wireOp",EDGE,"0a55f61a-76dd-4ac3-9223-154b0b1f7dfb.0");var subQ1=sQuery(id+"F0.wireOp",EDGE,"9343b0c3-cd2f-487d-bd13-aee8d7f259e0.0");var subQ2=makeQuery(id+"F0.imprint","INTERSECT",VERTEX,{"derivedFrom":[subQ1,subQ0]});Q57=makeQuery(id+"F0.imprint","IMPRINT",FACE,{"disambiguationData":[TD([[makeQuery(id+"F0.imprint","IMPRINT",EDGE,{"disambiguationData":[TD([[subQ2,-1.0]])],"derivedFrom":subQ1}),1.0]])]});}
            var Q58;
            {var subQ0=sQuery(id+"F0.wireOp",EDGE,"854f07df-45a9-419d-971c-554534df12f4.0");var subQ1=sQuery(id+"F0.wireOp",EDGE,"23e37434-4ebb-4948-80c8-8d17bba51405.0");var subQ2=makeQuery(id+"F0.imprint","INTERSECT",VERTEX,{"derivedFrom":[subQ1,subQ0]});Q58=makeQuery(id+"F0.imprint","IMPRINT",FACE,{"disambiguationData":[TD([[makeQuery(id+"F0.imprint","IMPRINT",EDGE,{"disambiguationData":[TD([[subQ2,1.0]])],"derivedFrom":subQ1}),-1.0]])]});}
            var Q59;
            {var subQ0=sQuery(id+"F0.wireOp",EDGE,"0a55f61a-76dd-4ac3-9223-154b0b1f7dfb.0");var subQ1=sQuery(id+"F0.wireOp",EDGE,"bdac1eed-a409-4cee-9b7b-61454a391d7d.0");var subQ2=makeQuery(id+"F0.imprint","INTERSECT",VERTEX,{"derivedFrom":[subQ1,subQ0]});Q59=makeQuery(id+"F0.imprint","IMPRINT",FACE,{"disambiguationData":[TD([[makeQuery(id+"F0.imprint","IMPRINT",EDGE,{"disambiguationData":[TD([[subQ2,-1.0]])],"derivedFrom":subQ1}),-1.0]])]});}
            var Q60;
            {var subQ0=sQuery(id+"F0.wireOp",EDGE,"a21ffa6c-e3b5-4756-9eef-63544e5bc852.0");var subQ1=sQuery(id+"F0.wireOp",EDGE,"bdac1eed-a409-4cee-9b7b-61454a391d7d.0");var subQ2=makeQuery(id+"F0.imprint","INTERSECT",VERTEX,{"derivedFrom":[subQ1,subQ0]});Q60=makeQuery(id+"F0.imprint","IMPRINT",FACE,{"disambiguationData":[TD([[makeQuery(id+"F0.imprint","IMPRINT",EDGE,{"disambiguationData":[TD([[subQ2,-1.0]])],"derivedFrom":subQ1}),-1.0]])]});}
            var Q61;
            {var subQ0=sQuery(id+"F0.wireOp",EDGE,"a21ffa6c-e3b5-4756-9eef-63544e5bc852.0");var subQ1=sQuery(id+"F0.wireOp",EDGE,"a62689d6-4df4-411d-a8de-d30e4e7abbb4.0");var subQ2=makeQuery(id+"F0.imprint","INTERSECT",VERTEX,{"derivedFrom":[subQ1,subQ0]});Q61=makeQuery(id+"F0.imprint","IMPRINT",FACE,{"disambiguationData":[TD([[makeQuery(id+"F0.imprint","IMPRINT",EDGE,{"disambiguationData":[TD([[subQ2,-1.0]])],"derivedFrom":subQ1}),-1.0]])]});}
            var Q62;
            {var subQ0=sQuery(id+"F0.wireOp",EDGE,"a21ffa6c-e3b5-4756-9eef-63544e5bc852.0");var subQ1=sQuery(id+"F0.wireOp",EDGE,"862523a1-1db9-4ec9-a786-b55df2c1a98e.0");var subQ2=makeQuery(id+"F0.imprint","INTERSECT",VERTEX,{"derivedFrom":[subQ1,subQ0]});Q62=makeQuery(id+"F0.imprint","IMPRINT",FACE,{"disambiguationData":[TD([[makeQuery(id+"F0.imprint","IMPRINT",EDGE,{"disambiguationData":[TD([[subQ2,-1.0]])],"derivedFrom":subQ1}),-1.0]])]});}
            var Q63;
            {var subQ0=sQuery(id+"F0.wireOp",EDGE,"0a55f61a-76dd-4ac3-9223-154b0b1f7dfb.0");var subQ1=sQuery(id+"F0.wireOp",EDGE,"a62689d6-4df4-411d-a8de-d30e4e7abbb4.0");var subQ2=makeQuery(id+"F0.imprint","INTERSECT",VERTEX,{"derivedFrom":[subQ1,subQ0]});Q63=makeQuery(id+"F0.imprint","IMPRINT",FACE,{"disambiguationData":[TD([[makeQuery(id+"F0.imprint","IMPRINT",EDGE,{"disambiguationData":[TD([[subQ2,-1.0]])],"derivedFrom":subQ1}),-1.0]])]});}
            var Q64;
            {var subQ0=sQuery(id+"F0.wireOp",EDGE,"0a55f61a-76dd-4ac3-9223-154b0b1f7dfb.0");var subQ1=sQuery(id+"F0.wireOp",EDGE,"f9003588-73a7-42be-b55c-edd191297de8.0");var subQ2=makeQuery(id+"F0.imprint","INTERSECT",VERTEX,{"derivedFrom":[subQ1,subQ0]});Q64=makeQuery(id+"F0.imprint","IMPRINT",FACE,{"disambiguationData":[TD([[makeQuery(id+"F0.imprint","IMPRINT",EDGE,{"disambiguationData":[TD([[subQ2,-1.0]])],"derivedFrom":subQ1}),-1.0]])]});}
            var Q65;
            {var subQ0=sQuery(id+"F0.wireOp",EDGE,"854f07df-45a9-419d-971c-554534df12f4.0");var subQ1=sQuery(id+"F0.wireOp",EDGE,"f9003588-73a7-42be-b55c-edd191297de8.0");var subQ2=makeQuery(id+"F0.imprint","INTERSECT",VERTEX,{"derivedFrom":[subQ1,subQ0]});Q65=makeQuery(id+"F0.imprint","IMPRINT",FACE,{"disambiguationData":[TD([[makeQuery(id+"F0.imprint","IMPRINT",EDGE,{"disambiguationData":[TD([[subQ2,1.0]])],"derivedFrom":subQ1}),-1.0]])]});}
            var Q66;
            {var subQ0=sQuery(id+"F0.wireOp",EDGE,"681770c7-baf9-4a3d-b09d-7c4e2b6cc42b.0");var subQ1=sQuery(id+"F0.wireOp",EDGE,"f9003588-73a7-42be-b55c-edd191297de8.0");var subQ2=makeQuery(id+"F0.imprint","INTERSECT",VERTEX,{"derivedFrom":[subQ1,subQ0]});Q66=makeQuery(id+"F0.imprint","IMPRINT",FACE,{"disambiguationData":[TD([[makeQuery(id+"F0.imprint","IMPRINT",EDGE,{"disambiguationData":[TD([[subQ2,-1.0]])],"derivedFrom":subQ1}),-1.0]])]});}
            var Q67;
            {var subQ0=sQuery(id+"F0.wireOp",EDGE,"450db5bc-e2e3-4f88-b9d5-953014a2ba1e.0");var subQ1=sQuery(id+"F0.wireOp",EDGE,"f9003588-73a7-42be-b55c-edd191297de8.0");var subQ2=makeQuery(id+"F0.imprint","INTERSECT",VERTEX,{"derivedFrom":[subQ1,subQ0]});Q67=makeQuery(id+"F0.imprint","IMPRINT",FACE,{"disambiguationData":[TD([[makeQuery(id+"F0.imprint","IMPRINT",EDGE,{"disambiguationData":[TD([[subQ2,-1.0]])],"derivedFrom":subQ1}),-1.0]])]});}
            var Q68;
            {var subQ0=sQuery(id+"F0.wireOp",EDGE,"E6.0");var subQ1=sQuery(id+"F0.wireOp",EDGE,"E0.left");var subQ2=makeQuery(id+"F0.imprint","INTERSECT",VERTEX,{"derivedFrom":[subQ1,subQ0]});Q68=makeQuery(id+"F0.imprint","IMPRINT",FACE,{"disambiguationData":[TD([[makeQuery(id+"F0.imprint","IMPRINT",EDGE,{"disambiguationData":[TD([[subQ2,-1.0]])],"derivedFrom":subQ1}),1.0]])]});}
            var Q69;
            {var subQ0=sQuery(id+"F0.wireOp",EDGE,"E22.0");var subQ1=sQuery(id+"F0.wireOp",EDGE,"E6.0");var subQ2=makeQuery(id+"F0.imprint","INTERSECT",VERTEX,{"derivedFrom":[subQ1,subQ0]});Q69=makeQuery(id+"F0.imprint","IMPRINT",FACE,{"disambiguationData":[TD([[makeQuery(id+"F0.imprint","IMPRINT",EDGE,{"disambiguationData":[TD([[subQ2,-1.0]])],"derivedFrom":subQ1}),-1.0]])]});}
            var Q70;
            {var subQ0=sQuery(id+"F0.wireOp",EDGE,"E23.0");var subQ1=sQuery(id+"F0.wireOp",EDGE,"E8.0");var subQ2=makeQuery(id+"F0.imprint","INTERSECT",VERTEX,{"derivedFrom":[subQ1,subQ0]});Q70=makeQuery(id+"F0.imprint","IMPRINT",FACE,{"disambiguationData":[TD([[makeQuery(id+"F0.imprint","IMPRINT",EDGE,{"disambiguationData":[TD([[subQ2,-1.0]])],"derivedFrom":subQ1}),-1.0]])]});}
            var Q71;
            {var subQ0=sQuery(id+"F0.wireOp",EDGE,"E22.0");var subQ1=sQuery(id+"F0.wireOp",EDGE,"E8.0");var subQ2=makeQuery(id+"F0.imprint","INTERSECT",VERTEX,{"derivedFrom":[subQ1,subQ0]});Q71=makeQuery(id+"F0.imprint","IMPRINT",FACE,{"disambiguationData":[TD([[makeQuery(id+"F0.imprint","IMPRINT",EDGE,{"disambiguationData":[TD([[subQ2,-1.0]])],"derivedFrom":subQ1}),-1.0]])]});}
            var Q72;
            {var subQ0=sQuery(id+"F0.wireOp",EDGE,"E22.0");var subQ1=sQuery(id+"F0.wireOp",EDGE,"E10.0");var subQ2=makeQuery(id+"F0.imprint","INTERSECT",VERTEX,{"derivedFrom":[subQ1,subQ0]});Q72=makeQuery(id+"F0.imprint","IMPRINT",FACE,{"disambiguationData":[TD([[makeQuery(id+"F0.imprint","IMPRINT",EDGE,{"disambiguationData":[TD([[subQ2,-1.0]])],"derivedFrom":subQ1}),-1.0]])]});}
            var Q73;
            {var subQ0=sQuery(id+"F0.wireOp",EDGE,"E23.0");var subQ1=sQuery(id+"F0.wireOp",EDGE,"E12.0");var subQ2=makeQuery(id+"F0.imprint","INTERSECT",VERTEX,{"derivedFrom":[subQ1,subQ0]});Q73=makeQuery(id+"F0.imprint","IMPRINT",FACE,{"disambiguationData":[TD([[makeQuery(id+"F0.imprint","IMPRINT",EDGE,{"disambiguationData":[TD([[subQ2,-1.0]])],"derivedFrom":subQ1}),-1.0]])]});}
            var Q74;
            {var subQ0=sQuery(id+"F0.wireOp",EDGE,"E20.0");var subQ1=sQuery(id+"F0.wireOp",EDGE,"E6.0");var subQ2=makeQuery(id+"F0.imprint","INTERSECT",VERTEX,{"derivedFrom":[subQ1,subQ0]});Q74=makeQuery(id+"F0.imprint","IMPRINT",FACE,{"disambiguationData":[TD([[makeQuery(id+"F0.imprint","IMPRINT",EDGE,{"disambiguationData":[TD([[subQ2,-1.0]])],"derivedFrom":subQ1}),-1.0]])]});}
            var Q75;
            {var subQ0=sQuery(id+"F0.wireOp",EDGE,"E20.0");var subQ1=sQuery(id+"F0.wireOp",EDGE,"E8.0");var subQ2=makeQuery(id+"F0.imprint","INTERSECT",VERTEX,{"derivedFrom":[subQ1,subQ0]});Q75=makeQuery(id+"F0.imprint","IMPRINT",FACE,{"disambiguationData":[TD([[makeQuery(id+"F0.imprint","IMPRINT",EDGE,{"disambiguationData":[TD([[subQ2,-1.0]])],"derivedFrom":subQ1}),-1.0]])]});}
            var Q76;
            {var subQ0=sQuery(id+"F0.wireOp",EDGE,"E21.0");var subQ1=sQuery(id+"F0.wireOp",EDGE,"E8.0");var subQ2=makeQuery(id+"F0.imprint","INTERSECT",VERTEX,{"derivedFrom":[subQ1,subQ0]});Q76=makeQuery(id+"F0.imprint","IMPRINT",FACE,{"disambiguationData":[TD([[makeQuery(id+"F0.imprint","IMPRINT",EDGE,{"disambiguationData":[TD([[subQ2,-1.0]])],"derivedFrom":subQ1}),-1.0]])]});}
            var Q77;
            {var subQ0=sQuery(id+"F0.wireOp",EDGE,"E20.0");var subQ1=sQuery(id+"F0.wireOp",EDGE,"E10.0");var subQ2=makeQuery(id+"F0.imprint","INTERSECT",VERTEX,{"derivedFrom":[subQ1,subQ0]});Q77=makeQuery(id+"F0.imprint","IMPRINT",FACE,{"disambiguationData":[TD([[makeQuery(id+"F0.imprint","IMPRINT",EDGE,{"disambiguationData":[TD([[subQ2,-1.0]])],"derivedFrom":subQ1}),-1.0]])]});}
            var Q78;
            {var subQ0=sQuery(id+"F0.wireOp",EDGE,"E19.0");var subQ1=sQuery(id+"F0.wireOp",EDGE,"E8.0");var subQ2=makeQuery(id+"F0.imprint","INTERSECT",VERTEX,{"derivedFrom":[subQ1,subQ0]});Q78=makeQuery(id+"F0.imprint","IMPRINT",FACE,{"disambiguationData":[TD([[makeQuery(id+"F0.imprint","IMPRINT",EDGE,{"disambiguationData":[TD([[subQ2,-1.0]])],"derivedFrom":subQ1}),-1.0]])]});}
            var Q79;
            {var subQ0=sQuery(id+"F0.wireOp",EDGE,"E18.0");var subQ1=sQuery(id+"F0.wireOp",EDGE,"E8.0");var subQ2=makeQuery(id+"F0.imprint","INTERSECT",VERTEX,{"derivedFrom":[subQ1,subQ0]});Q79=makeQuery(id+"F0.imprint","IMPRINT",FACE,{"disambiguationData":[TD([[makeQuery(id+"F0.imprint","IMPRINT",EDGE,{"disambiguationData":[TD([[subQ2,-1.0]])],"derivedFrom":subQ1}),-1.0]])]});}
            var Q80;
            {var subQ0=sQuery(id+"F0.wireOp",EDGE,"E18.0");var subQ1=sQuery(id+"F0.wireOp",EDGE,"E6.0");var subQ2=makeQuery(id+"F0.imprint","INTERSECT",VERTEX,{"derivedFrom":[subQ1,subQ0]});Q80=makeQuery(id+"F0.imprint","IMPRINT",FACE,{"disambiguationData":[TD([[makeQuery(id+"F0.imprint","IMPRINT",EDGE,{"disambiguationData":[TD([[subQ2,-1.0]])],"derivedFrom":subQ1}),-1.0]])]});}
            var Q81;
            {var subQ0=sQuery(id+"F0.wireOp",EDGE,"E17.0");var subQ1=sQuery(id+"F0.wireOp",EDGE,"E8.0");var subQ2=makeQuery(id+"F0.imprint","INTERSECT",VERTEX,{"derivedFrom":[subQ1,subQ0]});Q81=makeQuery(id+"F0.imprint","IMPRINT",FACE,{"disambiguationData":[TD([[makeQuery(id+"F0.imprint","IMPRINT",EDGE,{"disambiguationData":[TD([[subQ2,-1.0]])],"derivedFrom":subQ1}),-1.0]])]});}
            var Q82;
            {var subQ0=sQuery(id+"F0.wireOp",EDGE,"E18.0");var subQ1=sQuery(id+"F0.wireOp",EDGE,"E10.0");var subQ2=makeQuery(id+"F0.imprint","INTERSECT",VERTEX,{"derivedFrom":[subQ1,subQ0]});Q82=makeQuery(id+"F0.imprint","IMPRINT",FACE,{"disambiguationData":[TD([[makeQuery(id+"F0.imprint","IMPRINT",EDGE,{"disambiguationData":[TD([[subQ2,-1.0]])],"derivedFrom":subQ1}),-1.0]])]});}
            var Q83;
            {var subQ0=sQuery(id+"F0.wireOp",EDGE,"E16.0");var subQ1=sQuery(id+"F0.wireOp",EDGE,"E6.0");var subQ2=makeQuery(id+"F0.imprint","INTERSECT",VERTEX,{"derivedFrom":[subQ1,subQ0]});Q83=makeQuery(id+"F0.imprint","IMPRINT",FACE,{"disambiguationData":[TD([[makeQuery(id+"F0.imprint","IMPRINT",EDGE,{"disambiguationData":[TD([[subQ2,-1.0]])],"derivedFrom":subQ1}),-1.0]])]});}
            var Q84;
            {var subQ0=sQuery(id+"F0.wireOp",EDGE,"E15.0");var subQ1=sQuery(id+"F0.wireOp",EDGE,"E8.0");var subQ2=makeQuery(id+"F0.imprint","INTERSECT",VERTEX,{"derivedFrom":[subQ1,subQ0]});Q84=makeQuery(id+"F0.imprint","IMPRINT",FACE,{"disambiguationData":[TD([[makeQuery(id+"F0.imprint","IMPRINT",EDGE,{"disambiguationData":[TD([[subQ2,-1.0]])],"derivedFrom":subQ1}),-1.0]])]});}
            var Q85;
            {var subQ0=sQuery(id+"F0.wireOp",EDGE,"E16.0");var subQ1=sQuery(id+"F0.wireOp",EDGE,"E8.0");var subQ2=makeQuery(id+"F0.imprint","INTERSECT",VERTEX,{"derivedFrom":[subQ1,subQ0]});Q85=makeQuery(id+"F0.imprint","IMPRINT",FACE,{"disambiguationData":[TD([[makeQuery(id+"F0.imprint","IMPRINT",EDGE,{"disambiguationData":[TD([[subQ2,-1.0]])],"derivedFrom":subQ1}),-1.0]])]});}
            var Q86;
            {var subQ0=sQuery(id+"F0.wireOp",EDGE,"E16.0");var subQ1=sQuery(id+"F0.wireOp",EDGE,"E10.0");var subQ2=makeQuery(id+"F0.imprint","INTERSECT",VERTEX,{"derivedFrom":[subQ1,subQ0]});Q86=makeQuery(id+"F0.imprint","IMPRINT",FACE,{"disambiguationData":[TD([[makeQuery(id+"F0.imprint","IMPRINT",EDGE,{"disambiguationData":[TD([[subQ2,-1.0]])],"derivedFrom":subQ1}),-1.0]])]});}
            var Q87;
            {var subQ0=sQuery(id+"F0.wireOp",EDGE,"E15.0");var subQ1=sQuery(id+"F0.wireOp",EDGE,"E12.0");var subQ2=makeQuery(id+"F0.imprint","INTERSECT",VERTEX,{"derivedFrom":[subQ1,subQ0]});Q87=makeQuery(id+"F0.imprint","IMPRINT",FACE,{"disambiguationData":[TD([[makeQuery(id+"F0.imprint","IMPRINT",EDGE,{"disambiguationData":[TD([[subQ2,-1.0]])],"derivedFrom":subQ1}),-1.0]])]});}
            var Q88;
            {var subQ0=sQuery(id+"F0.wireOp",EDGE,"E17.0");var subQ1=sQuery(id+"F0.wireOp",EDGE,"E12.0");var subQ2=makeQuery(id+"F0.imprint","INTERSECT",VERTEX,{"derivedFrom":[subQ1,subQ0]});Q88=makeQuery(id+"F0.imprint","IMPRINT",FACE,{"disambiguationData":[TD([[makeQuery(id+"F0.imprint","IMPRINT",EDGE,{"disambiguationData":[TD([[subQ2,-1.0]])],"derivedFrom":subQ1}),-1.0]])]});}
            var Q89;
            {var subQ0=sQuery(id+"F0.wireOp",EDGE,"E16.0");var subQ1=sQuery(id+"F0.wireOp",EDGE,"E12.0");var subQ2=makeQuery(id+"F0.imprint","INTERSECT",VERTEX,{"derivedFrom":[subQ1,subQ0]});Q89=makeQuery(id+"F0.imprint","IMPRINT",FACE,{"disambiguationData":[TD([[makeQuery(id+"F0.imprint","IMPRINT",EDGE,{"disambiguationData":[TD([[subQ2,-1.0]])],"derivedFrom":subQ1}),-1.0]])]});}
            var Q90;
            {var subQ0=sQuery(id+"F0.wireOp",EDGE,"E16.0");var subQ1=sQuery(id+"F0.wireOp",EDGE,"E9.0");var subQ2=makeQuery(id+"F0.imprint","INTERSECT",VERTEX,{"derivedFrom":[subQ1,subQ0]});Q90=makeQuery(id+"F0.imprint","IMPRINT",FACE,{"disambiguationData":[TD([[makeQuery(id+"F0.imprint","IMPRINT",EDGE,{"disambiguationData":[TD([[subQ2,-1.0]])],"derivedFrom":subQ1}),1.0]])]});}
            var Q91;
            {var subQ0=sQuery(id+"F0.wireOp",EDGE,"E16.0");var subQ1=sQuery(id+"F0.wireOp",EDGE,"E7.0");var subQ2=makeQuery(id+"F0.imprint","INTERSECT",VERTEX,{"derivedFrom":[subQ1,subQ0]});Q91=makeQuery(id+"F0.imprint","IMPRINT",FACE,{"disambiguationData":[TD([[makeQuery(id+"F0.imprint","IMPRINT",EDGE,{"disambiguationData":[TD([[subQ2,-1.0]])],"derivedFrom":subQ1}),1.0]])]});}
            var Q92;
            {var subQ0=sQuery(id+"F0.wireOp",EDGE,"E15.0");var subQ1=sQuery(id+"F0.wireOp",EDGE,"E9.0");var subQ2=makeQuery(id+"F0.imprint","INTERSECT",VERTEX,{"derivedFrom":[subQ1,subQ0]});Q92=makeQuery(id+"F0.imprint","IMPRINT",FACE,{"disambiguationData":[TD([[makeQuery(id+"F0.imprint","IMPRINT",EDGE,{"disambiguationData":[TD([[subQ2,-1.0]])],"derivedFrom":subQ1}),1.0]])]});}
            var Q93;
            {var subQ0=sQuery(id+"F0.wireOp",EDGE,"E16.0");var subQ1=sQuery(id+"F0.wireOp",EDGE,"E11.0");var subQ2=makeQuery(id+"F0.imprint","INTERSECT",VERTEX,{"derivedFrom":[subQ1,subQ0]});Q93=makeQuery(id+"F0.imprint","IMPRINT",FACE,{"disambiguationData":[TD([[makeQuery(id+"F0.imprint","IMPRINT",EDGE,{"disambiguationData":[TD([[subQ2,-1.0]])],"derivedFrom":subQ1}),1.0]])]});}
            var Q94;
            {var subQ0=sQuery(id+"F0.wireOp",EDGE,"E17.0");var subQ1=sQuery(id+"F0.wireOp",EDGE,"E9.0");var subQ2=makeQuery(id+"F0.imprint","INTERSECT",VERTEX,{"derivedFrom":[subQ1,subQ0]});Q94=makeQuery(id+"F0.imprint","IMPRINT",FACE,{"disambiguationData":[TD([[makeQuery(id+"F0.imprint","IMPRINT",EDGE,{"disambiguationData":[TD([[subQ2,-1.0]])],"derivedFrom":subQ1}),1.0]])]});}
            var Q95;
            {var subQ0=sQuery(id+"F0.wireOp",EDGE,"E18.0");var subQ1=sQuery(id+"F0.wireOp",EDGE,"E9.0");var subQ2=makeQuery(id+"F0.imprint","INTERSECT",VERTEX,{"derivedFrom":[subQ1,subQ0]});Q95=makeQuery(id+"F0.imprint","IMPRINT",FACE,{"disambiguationData":[TD([[makeQuery(id+"F0.imprint","IMPRINT",EDGE,{"disambiguationData":[TD([[subQ2,-1.0]])],"derivedFrom":subQ1}),1.0]])]});}
            var Q96;
            {var subQ0=sQuery(id+"F0.wireOp",EDGE,"E18.0");var subQ1=sQuery(id+"F0.wireOp",EDGE,"E11.0");var subQ2=makeQuery(id+"F0.imprint","INTERSECT",VERTEX,{"derivedFrom":[subQ1,subQ0]});Q96=makeQuery(id+"F0.imprint","IMPRINT",FACE,{"disambiguationData":[TD([[makeQuery(id+"F0.imprint","IMPRINT",EDGE,{"disambiguationData":[TD([[subQ2,-1.0]])],"derivedFrom":subQ1}),1.0]])]});}
            var Q97;
            {var subQ0=sQuery(id+"F0.wireOp",EDGE,"E18.0");var subQ1=sQuery(id+"F0.wireOp",EDGE,"E7.0");var subQ2=makeQuery(id+"F0.imprint","INTERSECT",VERTEX,{"derivedFrom":[subQ1,subQ0]});Q97=makeQuery(id+"F0.imprint","IMPRINT",FACE,{"disambiguationData":[TD([[makeQuery(id+"F0.imprint","IMPRINT",EDGE,{"disambiguationData":[TD([[subQ2,-1.0]])],"derivedFrom":subQ1}),1.0]])]});}
            var Q98;
            {var subQ0=sQuery(id+"F0.wireOp",EDGE,"E19.0");var subQ1=sQuery(id+"F0.wireOp",EDGE,"E9.0");var subQ2=makeQuery(id+"F0.imprint","INTERSECT",VERTEX,{"derivedFrom":[subQ1,subQ0]});Q98=makeQuery(id+"F0.imprint","IMPRINT",FACE,{"disambiguationData":[TD([[makeQuery(id+"F0.imprint","IMPRINT",EDGE,{"disambiguationData":[TD([[subQ2,-1.0]])],"derivedFrom":subQ1}),1.0]])]});}
            var Q99;
            {var subQ0=sQuery(id+"F0.wireOp",EDGE,"E20.0");var subQ1=sQuery(id+"F0.wireOp",EDGE,"E9.0");var subQ2=makeQuery(id+"F0.imprint","INTERSECT",VERTEX,{"derivedFrom":[subQ1,subQ0]});Q99=makeQuery(id+"F0.imprint","IMPRINT",FACE,{"disambiguationData":[TD([[makeQuery(id+"F0.imprint","IMPRINT",EDGE,{"disambiguationData":[TD([[subQ2,-1.0]])],"derivedFrom":subQ1}),1.0]])]});}
            var Q100;
            {var subQ0=sQuery(id+"F0.wireOp",EDGE,"E20.0");var subQ1=sQuery(id+"F0.wireOp",EDGE,"E11.0");var subQ2=makeQuery(id+"F0.imprint","INTERSECT",VERTEX,{"derivedFrom":[subQ1,subQ0]});Q100=makeQuery(id+"F0.imprint","IMPRINT",FACE,{"disambiguationData":[TD([[makeQuery(id+"F0.imprint","IMPRINT",EDGE,{"disambiguationData":[TD([[subQ2,-1.0]])],"derivedFrom":subQ1}),1.0]])]});}
            var Q101;
            {var subQ0=sQuery(id+"F0.wireOp",EDGE,"E21.0");var subQ1=sQuery(id+"F0.wireOp",EDGE,"E9.0");var subQ2=makeQuery(id+"F0.imprint","INTERSECT",VERTEX,{"derivedFrom":[subQ1,subQ0]});Q101=makeQuery(id+"F0.imprint","IMPRINT",FACE,{"disambiguationData":[TD([[makeQuery(id+"F0.imprint","IMPRINT",EDGE,{"disambiguationData":[TD([[subQ2,-1.0]])],"derivedFrom":subQ1}),1.0]])]});}
            var Q102;
            {var subQ0=sQuery(id+"F0.wireOp",EDGE,"E20.0");var subQ1=sQuery(id+"F0.wireOp",EDGE,"E7.0");var subQ2=makeQuery(id+"F0.imprint","INTERSECT",VERTEX,{"derivedFrom":[subQ1,subQ0]});Q102=makeQuery(id+"F0.imprint","IMPRINT",FACE,{"disambiguationData":[TD([[makeQuery(id+"F0.imprint","IMPRINT",EDGE,{"disambiguationData":[TD([[subQ2,-1.0]])],"derivedFrom":subQ1}),1.0]])]});}
            var Q103;
            {var subQ0=sQuery(id+"F0.wireOp",EDGE,"E22.0");var subQ1=sQuery(id+"F0.wireOp",EDGE,"E7.0");var subQ2=makeQuery(id+"F0.imprint","INTERSECT",VERTEX,{"derivedFrom":[subQ1,subQ0]});Q103=makeQuery(id+"F0.imprint","IMPRINT",FACE,{"disambiguationData":[TD([[makeQuery(id+"F0.imprint","IMPRINT",EDGE,{"disambiguationData":[TD([[subQ2,-1.0]])],"derivedFrom":subQ1}),1.0]])]});}
            var Q104;
            {var subQ0=sQuery(id+"F0.wireOp",EDGE,"E22.0");var subQ1=sQuery(id+"F0.wireOp",EDGE,"E9.0");var subQ2=makeQuery(id+"F0.imprint","INTERSECT",VERTEX,{"derivedFrom":[subQ1,subQ0]});Q104=makeQuery(id+"F0.imprint","IMPRINT",FACE,{"disambiguationData":[TD([[makeQuery(id+"F0.imprint","IMPRINT",EDGE,{"disambiguationData":[TD([[subQ2,-1.0]])],"derivedFrom":subQ1}),1.0]])]});}
            var Q105;
            {var subQ0=sQuery(id+"F0.wireOp",EDGE,"E22.0");var subQ1=sQuery(id+"F0.wireOp",EDGE,"E11.0");var subQ2=makeQuery(id+"F0.imprint","INTERSECT",VERTEX,{"derivedFrom":[subQ1,subQ0]});Q105=makeQuery(id+"F0.imprint","IMPRINT",FACE,{"disambiguationData":[TD([[makeQuery(id+"F0.imprint","IMPRINT",EDGE,{"disambiguationData":[TD([[subQ2,-1.0]])],"derivedFrom":subQ1}),1.0]])]});}
            var Q106;
            {var subQ0=sQuery(id+"F0.wireOp",EDGE,"E23.0");var subQ1=sQuery(id+"F0.wireOp",EDGE,"E9.0");var subQ2=makeQuery(id+"F0.imprint","INTERSECT",VERTEX,{"derivedFrom":[subQ1,subQ0]});Q106=makeQuery(id+"F0.imprint","IMPRINT",FACE,{"disambiguationData":[TD([[makeQuery(id+"F0.imprint","IMPRINT",EDGE,{"disambiguationData":[TD([[subQ2,-1.0]])],"derivedFrom":subQ1}),1.0]])]});}
            var Q107;
            {var subQ0=sQuery(id+"F0.wireOp",EDGE,"E22.0");var subQ1=sQuery(id+"F0.wireOp",EDGE,"E12.0");var subQ2=makeQuery(id+"F0.imprint","INTERSECT",VERTEX,{"derivedFrom":[subQ1,subQ0]});Q107=makeQuery(id+"F0.imprint","IMPRINT",FACE,{"disambiguationData":[TD([[makeQuery(id+"F0.imprint","IMPRINT",EDGE,{"disambiguationData":[TD([[subQ2,-1.0]])],"derivedFrom":subQ1}),-1.0]])]});}
            var Q108;
            {var subQ0=sQuery(id+"F0.wireOp",EDGE,"E21.0");var subQ1=sQuery(id+"F0.wireOp",EDGE,"E12.0");var subQ2=makeQuery(id+"F0.imprint","INTERSECT",VERTEX,{"derivedFrom":[subQ1,subQ0]});Q108=makeQuery(id+"F0.imprint","IMPRINT",FACE,{"disambiguationData":[TD([[makeQuery(id+"F0.imprint","IMPRINT",EDGE,{"disambiguationData":[TD([[subQ2,-1.0]])],"derivedFrom":subQ1}),-1.0]])]});}
            var Q109;
            {var subQ0=sQuery(id+"F0.wireOp",EDGE,"E20.0");var subQ1=sQuery(id+"F0.wireOp",EDGE,"E12.0");var subQ2=makeQuery(id+"F0.imprint","INTERSECT",VERTEX,{"derivedFrom":[subQ1,subQ0]});Q109=makeQuery(id+"F0.imprint","IMPRINT",FACE,{"disambiguationData":[TD([[makeQuery(id+"F0.imprint","IMPRINT",EDGE,{"disambiguationData":[TD([[subQ2,-1.0]])],"derivedFrom":subQ1}),-1.0]])]});}
            var Q110;
            {var subQ0=sQuery(id+"F0.wireOp",EDGE,"E19.0");var subQ1=sQuery(id+"F0.wireOp",EDGE,"E12.0");var subQ2=makeQuery(id+"F0.imprint","INTERSECT",VERTEX,{"derivedFrom":[subQ1,subQ0]});Q110=makeQuery(id+"F0.imprint","IMPRINT",FACE,{"disambiguationData":[TD([[makeQuery(id+"F0.imprint","IMPRINT",EDGE,{"disambiguationData":[TD([[subQ2,-1.0]])],"derivedFrom":subQ1}),-1.0]])]});}
            var Q111;
            {var subQ0=sQuery(id+"F0.wireOp",EDGE,"E18.0");var subQ1=sQuery(id+"F0.wireOp",EDGE,"E12.0");var subQ2=makeQuery(id+"F0.imprint","INTERSECT",VERTEX,{"derivedFrom":[subQ1,subQ0]});Q111=makeQuery(id+"F0.imprint","IMPRINT",FACE,{"disambiguationData":[TD([[makeQuery(id+"F0.imprint","IMPRINT",EDGE,{"disambiguationData":[TD([[subQ2,-1.0]])],"derivedFrom":subQ1}),-1.0]])]});}
            extrude(context, id + "F1", {"entities" : qUnion([Q0, Q1, Q2, Q3, Q4, Q5, Q6, Q7, Q8, Q9, Q10, Q11, Q12, Q13, Q14, Q15, Q16, Q17, Q18, Q19, Q20, Q21, Q22, Q23, Q24, Q25, Q26, Q27, Q28, Q29, Q30, Q31, Q32, Q33, Q34, Q35, Q36, Q37, Q38, Q39, Q40, Q41, Q42, Q43, Q44, Q45, Q46, Q47, Q48, Q49, Q50, Q51, Q52, Q53, Q54, Q55, Q56, Q57, Q58, Q59, Q60, Q61, Q62, Q63, Q64, Q65, Q66, Q67, Q68, Q69, Q70, Q71, Q72, Q73, Q74, Q75, Q76, Q77, Q78, Q79, Q80, Q81, Q82, Q83, Q84, Q85, Q86, Q87, Q88, Q89, Q90, Q91, Q92, Q93, Q94, Q95, Q96, Q97, Q98, Q99, Q100, Q101, Q102, Q103, Q104, Q105, Q106, Q107, Q108, Q109, Q110, Q111]), "depth" : 8.4 * mm, "offsetDistance" : 25 * mm});
        }
        {
            var Q0;
            {var subQ0=sQuery(id+"F0.wireOp",EDGE,"919ec9c0-a23d-4d93-b64b-cbbe13223f10.0");Q0=makeQuery(id+"F1.opExtrude","CAP_EDGE",EDGE,{"disambiguationData":[OSD([subQ0]),TDD([makeQuery(id+"F0.imprint","IMPRINT",EDGE,{"disambiguationData":[TD([[makeQuery(id+"F0.imprint","INTERSECT",VERTEX,{"derivedFrom":[sQuery(id+"F0.wireOp",EDGE,"3e5cf576-49dc-4465-ad3e-ca1242db3cf5.0"),subQ0]}),-1.0]])],"derivedFrom":subQ0})])],"isStart":false});}
            var Q1;
            {var subQ0=sQuery(id+"F0.wireOp",EDGE,"919ec9c0-a23d-4d93-b64b-cbbe13223f10.0");Q1=makeQuery(id+"F1.opExtrude","CAP_EDGE",EDGE,{"disambiguationData":[OSD([subQ0]),TDD([makeQuery(id+"F0.imprint","IMPRINT",EDGE,{"disambiguationData":[TD([[makeQuery(id+"F0.imprint","INTERSECT",VERTEX,{"derivedFrom":[sQuery(id+"F0.wireOp",EDGE,"9343b0c3-cd2f-487d-bd13-aee8d7f259e0.0"),subQ0]}),-1.0]])],"derivedFrom":subQ0})])],"isStart":false});}
            var Q2;
            {var subQ0=sQuery(id+"F0.wireOp",EDGE,"450db5bc-e2e3-4f88-b9d5-953014a2ba1e.0");Q2=makeQuery(id+"F1.opExtrude","CAP_EDGE",EDGE,{"disambiguationData":[OSD([subQ0]),TDD([makeQuery(id+"F0.imprint","IMPRINT",EDGE,{"disambiguationData":[TD([[makeQuery(id+"F0.imprint","INTERSECT",VERTEX,{"derivedFrom":[sQuery(id+"F0.wireOp",EDGE,"3e5cf576-49dc-4465-ad3e-ca1242db3cf5.0"),subQ0]}),-1.0]])],"derivedFrom":subQ0})])],"isStart":false});}
            var Q3;
            {var subQ0=sQuery(id+"F0.wireOp",EDGE,"450db5bc-e2e3-4f88-b9d5-953014a2ba1e.0");Q3=makeQuery(id+"F1.opExtrude","CAP_EDGE",EDGE,{"disambiguationData":[OSD([subQ0]),TDD([makeQuery(id+"F0.imprint","IMPRINT",EDGE,{"disambiguationData":[TD([[makeQuery(id+"F0.imprint","INTERSECT",VERTEX,{"derivedFrom":[sQuery(id+"F0.wireOp",EDGE,"9343b0c3-cd2f-487d-bd13-aee8d7f259e0.0"),subQ0]}),-1.0]])],"derivedFrom":subQ0})])],"isStart":false});}
            var Q4;
            {var subQ0=sQuery(id+"F0.wireOp",EDGE,"a21ffa6c-e3b5-4756-9eef-63544e5bc852.0");Q4=makeQuery(id+"F1.opExtrude","CAP_EDGE",EDGE,{"disambiguationData":[OSD([subQ0]),TDD([makeQuery(id+"F0.imprint","IMPRINT",EDGE,{"disambiguationData":[TD([[makeQuery(id+"F0.imprint","INTERSECT",VERTEX,{"derivedFrom":[sQuery(id+"F0.wireOp",EDGE,"3e5cf576-49dc-4465-ad3e-ca1242db3cf5.0"),subQ0]}),-1.0]])],"derivedFrom":subQ0})])],"isStart":false});}
            var Q5;
            {var subQ0=sQuery(id+"F0.wireOp",EDGE,"681770c7-baf9-4a3d-b09d-7c4e2b6cc42b.0");Q5=makeQuery(id+"F1.opExtrude","CAP_EDGE",EDGE,{"disambiguationData":[OSD([subQ0]),TDD([makeQuery(id+"F0.imprint","IMPRINT",EDGE,{"disambiguationData":[TD([[makeQuery(id+"F0.imprint","INTERSECT",VERTEX,{"derivedFrom":[sQuery(id+"F0.wireOp",EDGE,"3e5cf576-49dc-4465-ad3e-ca1242db3cf5.0"),subQ0]}),-1.0]])],"derivedFrom":subQ0})])],"isStart":false});}
            var Q6;
            {var subQ0=sQuery(id+"F0.wireOp",EDGE,"0a55f61a-76dd-4ac3-9223-154b0b1f7dfb.0");Q6=makeQuery(id+"F1.opExtrude","CAP_EDGE",EDGE,{"disambiguationData":[OSD([subQ0]),TDD([makeQuery(id+"F0.imprint","IMPRINT",EDGE,{"disambiguationData":[TD([[makeQuery(id+"F0.imprint","INTERSECT",VERTEX,{"derivedFrom":[sQuery(id+"F0.wireOp",EDGE,"3e5cf576-49dc-4465-ad3e-ca1242db3cf5.0"),subQ0]}),-1.0]])],"derivedFrom":subQ0})])],"isStart":false});}
            var Q7;
            {var subQ0=sQuery(id+"F0.wireOp",EDGE,"0c15ec7b-9e92-4eb4-8615-29722b4b26f3.0");Q7=makeQuery(id+"F1.opExtrude","CAP_EDGE",EDGE,{"disambiguationData":[OSD([subQ0]),TDD([makeQuery(id+"F0.imprint","IMPRINT",EDGE,{"disambiguationData":[TD([[makeQuery(id+"F0.imprint","INTERSECT",VERTEX,{"derivedFrom":[sQuery(id+"F0.wireOp",EDGE,"3e5cf576-49dc-4465-ad3e-ca1242db3cf5.0"),subQ0]}),-1.0]])],"derivedFrom":subQ0})])],"isStart":false});}
            var Q8;
            {var subQ0=sQuery(id+"F0.wireOp",EDGE,"0c15ec7b-9e92-4eb4-8615-29722b4b26f3.0");Q8=makeQuery(id+"F1.opExtrude","CAP_EDGE",EDGE,{"disambiguationData":[OSD([subQ0]),TDD([makeQuery(id+"F0.imprint","IMPRINT",EDGE,{"disambiguationData":[TD([[makeQuery(id+"F0.imprint","INTERSECT",VERTEX,{"derivedFrom":[sQuery(id+"F0.wireOp",EDGE,"9343b0c3-cd2f-487d-bd13-aee8d7f259e0.0"),subQ0]}),-1.0]])],"derivedFrom":subQ0})])],"isStart":false});}
            var Q9;
            {var subQ0=sQuery(id+"F0.wireOp",EDGE,"0a55f61a-76dd-4ac3-9223-154b0b1f7dfb.0");Q9=makeQuery(id+"F1.opExtrude","CAP_EDGE",EDGE,{"disambiguationData":[OSD([subQ0]),TDD([makeQuery(id+"F0.imprint","IMPRINT",EDGE,{"disambiguationData":[TD([[makeQuery(id+"F0.imprint","INTERSECT",VERTEX,{"derivedFrom":[sQuery(id+"F0.wireOp",EDGE,"9343b0c3-cd2f-487d-bd13-aee8d7f259e0.0"),subQ0]}),-1.0]])],"derivedFrom":subQ0})])],"isStart":false});}
            var Q10;
            {var subQ0=sQuery(id+"F0.wireOp",EDGE,"681770c7-baf9-4a3d-b09d-7c4e2b6cc42b.0");Q10=makeQuery(id+"F1.opExtrude","CAP_EDGE",EDGE,{"disambiguationData":[OSD([subQ0]),TDD([makeQuery(id+"F0.imprint","IMPRINT",EDGE,{"disambiguationData":[TD([[makeQuery(id+"F0.imprint","INTERSECT",VERTEX,{"derivedFrom":[sQuery(id+"F0.wireOp",EDGE,"9343b0c3-cd2f-487d-bd13-aee8d7f259e0.0"),subQ0]}),-1.0]])],"derivedFrom":subQ0})])],"isStart":false});}
            var Q11;
            {var subQ0=sQuery(id+"F0.wireOp",EDGE,"a21ffa6c-e3b5-4756-9eef-63544e5bc852.0");Q11=makeQuery(id+"F1.opExtrude","CAP_EDGE",EDGE,{"disambiguationData":[OSD([subQ0]),TDD([makeQuery(id+"F0.imprint","IMPRINT",EDGE,{"disambiguationData":[TD([[makeQuery(id+"F0.imprint","INTERSECT",VERTEX,{"derivedFrom":[sQuery(id+"F0.wireOp",EDGE,"9343b0c3-cd2f-487d-bd13-aee8d7f259e0.0"),subQ0]}),-1.0]])],"derivedFrom":subQ0})])],"isStart":false});}
            var Q12;
            {var subQ0=sQuery(id+"F0.wireOp",EDGE,"919ec9c0-a23d-4d93-b64b-cbbe13223f10.0");Q12=makeQuery(id+"F1.opExtrude","CAP_EDGE",EDGE,{"disambiguationData":[OSD([subQ0]),TDD([makeQuery(id+"F0.imprint","IMPRINT",EDGE,{"disambiguationData":[TD([[makeQuery(id+"F0.imprint","INTERSECT",VERTEX,{"derivedFrom":[sQuery(id+"F0.wireOp",EDGE,"bdac1eed-a409-4cee-9b7b-61454a391d7d.0"),subQ0]}),1.0]])],"derivedFrom":subQ0})])],"isStart":false});}
            var Q13;
            {var subQ0=sQuery(id+"F0.wireOp",EDGE,"919ec9c0-a23d-4d93-b64b-cbbe13223f10.0");Q13=makeQuery(id+"F1.opExtrude","CAP_EDGE",EDGE,{"disambiguationData":[OSD([subQ0]),TDD([makeQuery(id+"F0.imprint","IMPRINT",EDGE,{"disambiguationData":[TD([[makeQuery(id+"F0.imprint","INTERSECT",VERTEX,{"derivedFrom":[sQuery(id+"F0.wireOp",EDGE,"a62689d6-4df4-411d-a8de-d30e4e7abbb4.0"),subQ0]}),1.0]])],"derivedFrom":subQ0})])],"isStart":false});}
            var Q14;
            {var subQ0=sQuery(id+"F0.wireOp",EDGE,"919ec9c0-a23d-4d93-b64b-cbbe13223f10.0");Q14=makeQuery(id+"F1.opExtrude","CAP_EDGE",EDGE,{"disambiguationData":[OSD([subQ0]),TDD([makeQuery(id+"F0.imprint","IMPRINT",EDGE,{"disambiguationData":[TD([[makeQuery(id+"F0.imprint","INTERSECT",VERTEX,{"derivedFrom":[sQuery(id+"F0.wireOp",EDGE,"862523a1-1db9-4ec9-a786-b55df2c1a98e.0"),subQ0]}),1.0]])],"derivedFrom":subQ0})])],"isStart":false});}
            var Q15;
            {var subQ0=sQuery(id+"F0.wireOp",EDGE,"a21ffa6c-e3b5-4756-9eef-63544e5bc852.0");Q15=makeQuery(id+"F1.opExtrude","CAP_EDGE",EDGE,{"disambiguationData":[OSD([subQ0]),TDD([makeQuery(id+"F0.imprint","IMPRINT",EDGE,{"disambiguationData":[TD([[makeQuery(id+"F0.imprint","INTERSECT",VERTEX,{"derivedFrom":[sQuery(id+"F0.wireOp",EDGE,"862523a1-1db9-4ec9-a786-b55df2c1a98e.0"),subQ0]}),1.0]])],"derivedFrom":subQ0})])],"isStart":false});}
            var Q16;
            {var subQ0=sQuery(id+"F0.wireOp",EDGE,"a21ffa6c-e3b5-4756-9eef-63544e5bc852.0");Q16=makeQuery(id+"F1.opExtrude","CAP_EDGE",EDGE,{"disambiguationData":[OSD([subQ0]),TDD([makeQuery(id+"F0.imprint","IMPRINT",EDGE,{"disambiguationData":[TD([[makeQuery(id+"F0.imprint","INTERSECT",VERTEX,{"derivedFrom":[sQuery(id+"F0.wireOp",EDGE,"a62689d6-4df4-411d-a8de-d30e4e7abbb4.0"),subQ0]}),1.0]])],"derivedFrom":subQ0})])],"isStart":false});}
            var Q17;
            {var subQ0=sQuery(id+"F0.wireOp",EDGE,"a21ffa6c-e3b5-4756-9eef-63544e5bc852.0");Q17=makeQuery(id+"F1.opExtrude","CAP_EDGE",EDGE,{"disambiguationData":[OSD([subQ0]),TDD([makeQuery(id+"F0.imprint","IMPRINT",EDGE,{"disambiguationData":[TD([[makeQuery(id+"F0.imprint","INTERSECT",VERTEX,{"derivedFrom":[sQuery(id+"F0.wireOp",EDGE,"bdac1eed-a409-4cee-9b7b-61454a391d7d.0"),subQ0]}),1.0]])],"derivedFrom":subQ0})])],"isStart":false});}
            var Q18;
            {var subQ0=sQuery(id+"F0.wireOp",EDGE,"681770c7-baf9-4a3d-b09d-7c4e2b6cc42b.0");Q18=makeQuery(id+"F1.opExtrude","CAP_EDGE",EDGE,{"disambiguationData":[OSD([subQ0]),TDD([makeQuery(id+"F0.imprint","IMPRINT",EDGE,{"disambiguationData":[TD([[makeQuery(id+"F0.imprint","INTERSECT",VERTEX,{"derivedFrom":[sQuery(id+"F0.wireOp",EDGE,"bdac1eed-a409-4cee-9b7b-61454a391d7d.0"),subQ0]}),1.0]])],"derivedFrom":subQ0})])],"isStart":false});}
            var Q19;
            {var subQ0=sQuery(id+"F0.wireOp",EDGE,"681770c7-baf9-4a3d-b09d-7c4e2b6cc42b.0");Q19=makeQuery(id+"F1.opExtrude","CAP_EDGE",EDGE,{"disambiguationData":[OSD([subQ0]),TDD([makeQuery(id+"F0.imprint","IMPRINT",EDGE,{"disambiguationData":[TD([[makeQuery(id+"F0.imprint","INTERSECT",VERTEX,{"derivedFrom":[sQuery(id+"F0.wireOp",EDGE,"a62689d6-4df4-411d-a8de-d30e4e7abbb4.0"),subQ0]}),1.0]])],"derivedFrom":subQ0})])],"isStart":false});}
            var Q20;
            {var subQ0=sQuery(id+"F0.wireOp",EDGE,"450db5bc-e2e3-4f88-b9d5-953014a2ba1e.0");Q20=makeQuery(id+"F1.opExtrude","CAP_EDGE",EDGE,{"disambiguationData":[OSD([subQ0]),TDD([makeQuery(id+"F0.imprint","IMPRINT",EDGE,{"disambiguationData":[TD([[makeQuery(id+"F0.imprint","INTERSECT",VERTEX,{"derivedFrom":[sQuery(id+"F0.wireOp",EDGE,"862523a1-1db9-4ec9-a786-b55df2c1a98e.0"),subQ0]}),1.0]])],"derivedFrom":subQ0})])],"isStart":false});}
            var Q21;
            {var subQ0=sQuery(id+"F0.wireOp",EDGE,"450db5bc-e2e3-4f88-b9d5-953014a2ba1e.0");Q21=makeQuery(id+"F1.opExtrude","CAP_EDGE",EDGE,{"disambiguationData":[OSD([subQ0]),TDD([makeQuery(id+"F0.imprint","IMPRINT",EDGE,{"disambiguationData":[TD([[makeQuery(id+"F0.imprint","INTERSECT",VERTEX,{"derivedFrom":[sQuery(id+"F0.wireOp",EDGE,"a62689d6-4df4-411d-a8de-d30e4e7abbb4.0"),subQ0]}),1.0]])],"derivedFrom":subQ0})])],"isStart":false});}
            var Q22;
            {var subQ0=sQuery(id+"F0.wireOp",EDGE,"450db5bc-e2e3-4f88-b9d5-953014a2ba1e.0");Q22=makeQuery(id+"F1.opExtrude","CAP_EDGE",EDGE,{"disambiguationData":[OSD([subQ0]),TDD([makeQuery(id+"F0.imprint","IMPRINT",EDGE,{"disambiguationData":[TD([[makeQuery(id+"F0.imprint","INTERSECT",VERTEX,{"derivedFrom":[sQuery(id+"F0.wireOp",EDGE,"bdac1eed-a409-4cee-9b7b-61454a391d7d.0"),subQ0]}),1.0]])],"derivedFrom":subQ0})])],"isStart":false});}
            var Q23;
            {var subQ0=sQuery(id+"F0.wireOp",EDGE,"681770c7-baf9-4a3d-b09d-7c4e2b6cc42b.0");Q23=makeQuery(id+"F1.opExtrude","CAP_EDGE",EDGE,{"disambiguationData":[OSD([subQ0]),TDD([makeQuery(id+"F0.imprint","IMPRINT",EDGE,{"disambiguationData":[TD([[makeQuery(id+"F0.imprint","INTERSECT",VERTEX,{"derivedFrom":[sQuery(id+"F0.wireOp",EDGE,"862523a1-1db9-4ec9-a786-b55df2c1a98e.0"),subQ0]}),1.0]])],"derivedFrom":subQ0})])],"isStart":false});}
            var Q24;
            {var subQ0=sQuery(id+"F0.wireOp",EDGE,"0a55f61a-76dd-4ac3-9223-154b0b1f7dfb.0");Q24=makeQuery(id+"F1.opExtrude","CAP_EDGE",EDGE,{"disambiguationData":[OSD([subQ0]),TDD([makeQuery(id+"F0.imprint","IMPRINT",EDGE,{"disambiguationData":[TD([[makeQuery(id+"F0.imprint","INTERSECT",VERTEX,{"derivedFrom":[sQuery(id+"F0.wireOp",EDGE,"862523a1-1db9-4ec9-a786-b55df2c1a98e.0"),subQ0]}),1.0]])],"derivedFrom":subQ0})])],"isStart":false});}
            var Q25;
            {var subQ0=sQuery(id+"F0.wireOp",EDGE,"0c15ec7b-9e92-4eb4-8615-29722b4b26f3.0");Q25=makeQuery(id+"F1.opExtrude","CAP_EDGE",EDGE,{"disambiguationData":[OSD([subQ0]),TDD([makeQuery(id+"F0.imprint","IMPRINT",EDGE,{"disambiguationData":[TD([[makeQuery(id+"F0.imprint","INTERSECT",VERTEX,{"derivedFrom":[sQuery(id+"F0.wireOp",EDGE,"a62689d6-4df4-411d-a8de-d30e4e7abbb4.0"),subQ0]}),1.0]])],"derivedFrom":subQ0})])],"isStart":false});}
            var Q26;
            {var subQ0=sQuery(id+"F0.wireOp",EDGE,"0a55f61a-76dd-4ac3-9223-154b0b1f7dfb.0");Q26=makeQuery(id+"F1.opExtrude","CAP_EDGE",EDGE,{"disambiguationData":[OSD([subQ0]),TDD([makeQuery(id+"F0.imprint","IMPRINT",EDGE,{"disambiguationData":[TD([[makeQuery(id+"F0.imprint","INTERSECT",VERTEX,{"derivedFrom":[sQuery(id+"F0.wireOp",EDGE,"a62689d6-4df4-411d-a8de-d30e4e7abbb4.0"),subQ0]}),1.0]])],"derivedFrom":subQ0})])],"isStart":false});}
            var Q27;
            {var subQ0=sQuery(id+"F0.wireOp",EDGE,"0a55f61a-76dd-4ac3-9223-154b0b1f7dfb.0");Q27=makeQuery(id+"F1.opExtrude","CAP_EDGE",EDGE,{"disambiguationData":[OSD([subQ0]),TDD([makeQuery(id+"F0.imprint","IMPRINT",EDGE,{"disambiguationData":[TD([[makeQuery(id+"F0.imprint","INTERSECT",VERTEX,{"derivedFrom":[sQuery(id+"F0.wireOp",EDGE,"bdac1eed-a409-4cee-9b7b-61454a391d7d.0"),subQ0]}),1.0]])],"derivedFrom":subQ0})])],"isStart":false});}
            var Q28;
            {var subQ0=sQuery(id+"F0.wireOp",EDGE,"0c15ec7b-9e92-4eb4-8615-29722b4b26f3.0");Q28=makeQuery(id+"F1.opExtrude","CAP_EDGE",EDGE,{"disambiguationData":[OSD([subQ0]),TDD([makeQuery(id+"F0.imprint","IMPRINT",EDGE,{"disambiguationData":[TD([[makeQuery(id+"F0.imprint","INTERSECT",VERTEX,{"derivedFrom":[sQuery(id+"F0.wireOp",EDGE,"bdac1eed-a409-4cee-9b7b-61454a391d7d.0"),subQ0]}),1.0]])],"derivedFrom":subQ0})])],"isStart":false});}
            var Q29;
            {var subQ0=sQuery(id+"F0.wireOp",EDGE,"0c15ec7b-9e92-4eb4-8615-29722b4b26f3.0");Q29=makeQuery(id+"F1.opExtrude","CAP_EDGE",EDGE,{"disambiguationData":[OSD([subQ0]),TDD([makeQuery(id+"F0.imprint","IMPRINT",EDGE,{"disambiguationData":[TD([[makeQuery(id+"F0.imprint","INTERSECT",VERTEX,{"derivedFrom":[sQuery(id+"F0.wireOp",EDGE,"862523a1-1db9-4ec9-a786-b55df2c1a98e.0"),subQ0]}),1.0]])],"derivedFrom":subQ0})])],"isStart":false});}
            var Q30;
            Q30=makeQuery(id+"F1.opExtrude","CAP_EDGE",EDGE,{"disambiguationData":[OSD([sQuery(id+"F0.wireOp",EDGE,"FuuDZzWY-bjfK-R4eX-IGd3-e1CRavVGCmtP")])],"isStart":false});
            var Q31;
            {var subQ0=sQuery(id+"F0.wireOp",EDGE,"E8.0");Q31=makeQuery(id+"F1.opExtrude","CAP_EDGE",EDGE,{"disambiguationData":[OSD([subQ0]),TDD([makeQuery(id+"F0.imprint","IMPRINT",EDGE,{"disambiguationData":[TD([[makeQuery(id+"F0.imprint","INTERSECT",VERTEX,{"derivedFrom":[subQ0,sQuery(id+"F0.wireOp",EDGE,"E23.0")]}),-1.0]])],"derivedFrom":subQ0})])],"isStart":false});}
            var Q32;
            {var subQ0=sQuery(id+"F0.wireOp",EDGE,"E10.0");Q32=makeQuery(id+"F1.opExtrude","CAP_EDGE",EDGE,{"disambiguationData":[OSD([subQ0]),TDD([makeQuery(id+"F0.imprint","IMPRINT",EDGE,{"disambiguationData":[TD([[makeQuery(id+"F0.imprint","INTERSECT",VERTEX,{"derivedFrom":[subQ0,sQuery(id+"F0.wireOp",EDGE,"E23.0")]}),-1.0]])],"derivedFrom":subQ0})])],"isStart":false});}
            var Q33;
            {var subQ0=sQuery(id+"F0.wireOp",EDGE,"E12.0");Q33=makeQuery(id+"F1.opExtrude","CAP_EDGE",EDGE,{"disambiguationData":[OSD([subQ0]),TDD([makeQuery(id+"F0.imprint","IMPRINT",EDGE,{"disambiguationData":[TD([[makeQuery(id+"F0.imprint","INTERSECT",VERTEX,{"derivedFrom":[subQ0,sQuery(id+"F0.wireOp",EDGE,"E23.0")]}),-1.0]])],"derivedFrom":subQ0})])],"isStart":false});}
            var Q34;
            {var subQ0=sQuery(id+"F0.wireOp",EDGE,"E13.0");Q34=makeQuery(id+"F1.opExtrude","CAP_EDGE",EDGE,{"disambiguationData":[OSD([subQ0]),TDD([makeQuery(id+"F0.imprint","IMPRINT",EDGE,{"disambiguationData":[TD([[makeQuery(id+"F0.imprint","INTERSECT",VERTEX,{"derivedFrom":[subQ0,sQuery(id+"F0.wireOp",EDGE,"E23.0")]}),-1.0]])],"derivedFrom":subQ0})])],"isStart":false});}
            var Q35;
            {var subQ0=sQuery(id+"F0.wireOp",EDGE,"E13.0");Q35=makeQuery(id+"F1.opExtrude","CAP_EDGE",EDGE,{"disambiguationData":[OSD([subQ0]),TDD([makeQuery(id+"F0.imprint","IMPRINT",EDGE,{"disambiguationData":[TD([[makeQuery(id+"F0.imprint","INTERSECT",VERTEX,{"derivedFrom":[subQ0,sQuery(id+"F0.wireOp",EDGE,"E21.0")]}),-1.0]])],"derivedFrom":subQ0})])],"isStart":false});}
            var Q36;
            {var subQ0=sQuery(id+"F0.wireOp",EDGE,"E12.0");Q36=makeQuery(id+"F1.opExtrude","CAP_EDGE",EDGE,{"disambiguationData":[OSD([subQ0]),TDD([makeQuery(id+"F0.imprint","IMPRINT",EDGE,{"disambiguationData":[TD([[makeQuery(id+"F0.imprint","INTERSECT",VERTEX,{"derivedFrom":[subQ0,sQuery(id+"F0.wireOp",EDGE,"E21.0")]}),-1.0]])],"derivedFrom":subQ0})])],"isStart":false});}
            var Q37;
            {var subQ0=sQuery(id+"F0.wireOp",EDGE,"E10.0");Q37=makeQuery(id+"F1.opExtrude","CAP_EDGE",EDGE,{"disambiguationData":[OSD([subQ0]),TDD([makeQuery(id+"F0.imprint","IMPRINT",EDGE,{"disambiguationData":[TD([[makeQuery(id+"F0.imprint","INTERSECT",VERTEX,{"derivedFrom":[subQ0,sQuery(id+"F0.wireOp",EDGE,"E21.0")]}),-1.0]])],"derivedFrom":subQ0})])],"isStart":false});}
            var Q38;
            {var subQ0=sQuery(id+"F0.wireOp",EDGE,"E8.0");Q38=makeQuery(id+"F1.opExtrude","CAP_EDGE",EDGE,{"disambiguationData":[OSD([subQ0]),TDD([makeQuery(id+"F0.imprint","IMPRINT",EDGE,{"disambiguationData":[TD([[makeQuery(id+"F0.imprint","INTERSECT",VERTEX,{"derivedFrom":[subQ0,sQuery(id+"F0.wireOp",EDGE,"E21.0")]}),-1.0]])],"derivedFrom":subQ0})])],"isStart":false});}
            var Q39;
            {var subQ0=sQuery(id+"F0.wireOp",EDGE,"E10.0");Q39=makeQuery(id+"F1.opExtrude","CAP_EDGE",EDGE,{"disambiguationData":[OSD([subQ0]),TDD([makeQuery(id+"F0.imprint","IMPRINT",EDGE,{"disambiguationData":[TD([[makeQuery(id+"F0.imprint","INTERSECT",VERTEX,{"derivedFrom":[subQ0,sQuery(id+"F0.wireOp",EDGE,"E19.0")]}),-1.0]])],"derivedFrom":subQ0})])],"isStart":false});}
            var Q40;
            {var subQ0=sQuery(id+"F0.wireOp",EDGE,"E8.0");Q40=makeQuery(id+"F1.opExtrude","CAP_EDGE",EDGE,{"disambiguationData":[OSD([subQ0]),TDD([makeQuery(id+"F0.imprint","IMPRINT",EDGE,{"disambiguationData":[TD([[makeQuery(id+"F0.imprint","INTERSECT",VERTEX,{"derivedFrom":[subQ0,sQuery(id+"F0.wireOp",EDGE,"E19.0")]}),-1.0]])],"derivedFrom":subQ0})])],"isStart":false});}
            var Q41;
            {var subQ0=sQuery(id+"F0.wireOp",EDGE,"E8.0");Q41=makeQuery(id+"F1.opExtrude","CAP_EDGE",EDGE,{"disambiguationData":[OSD([subQ0]),TDD([makeQuery(id+"F0.imprint","IMPRINT",EDGE,{"disambiguationData":[TD([[makeQuery(id+"F0.imprint","INTERSECT",VERTEX,{"derivedFrom":[subQ0,sQuery(id+"F0.wireOp",EDGE,"E17.0")]}),-1.0]])],"derivedFrom":subQ0})])],"isStart":false});}
            var Q42;
            {var subQ0=sQuery(id+"F0.wireOp",EDGE,"E10.0");Q42=makeQuery(id+"F1.opExtrude","CAP_EDGE",EDGE,{"disambiguationData":[OSD([subQ0]),TDD([makeQuery(id+"F0.imprint","IMPRINT",EDGE,{"disambiguationData":[TD([[makeQuery(id+"F0.imprint","INTERSECT",VERTEX,{"derivedFrom":[subQ0,sQuery(id+"F0.wireOp",EDGE,"E17.0")]}),-1.0]])],"derivedFrom":subQ0})])],"isStart":false});}
            var Q43;
            {var subQ0=sQuery(id+"F0.wireOp",EDGE,"E13.0");Q43=makeQuery(id+"F1.opExtrude","CAP_EDGE",EDGE,{"disambiguationData":[OSD([subQ0]),TDD([makeQuery(id+"F0.imprint","IMPRINT",EDGE,{"disambiguationData":[TD([[makeQuery(id+"F0.imprint","INTERSECT",VERTEX,{"derivedFrom":[subQ0,sQuery(id+"F0.wireOp",EDGE,"E19.0")]}),-1.0]])],"derivedFrom":subQ0})])],"isStart":false});}
            var Q44;
            {var subQ0=sQuery(id+"F0.wireOp",EDGE,"E12.0");Q44=makeQuery(id+"F1.opExtrude","CAP_EDGE",EDGE,{"disambiguationData":[OSD([subQ0]),TDD([makeQuery(id+"F0.imprint","IMPRINT",EDGE,{"disambiguationData":[TD([[makeQuery(id+"F0.imprint","INTERSECT",VERTEX,{"derivedFrom":[subQ0,sQuery(id+"F0.wireOp",EDGE,"E19.0")]}),-1.0]])],"derivedFrom":subQ0})])],"isStart":false});}
            var Q45;
            {var subQ0=sQuery(id+"F0.wireOp",EDGE,"E9.0");Q45=makeQuery(id+"F1.opExtrude","CAP_EDGE",EDGE,{"disambiguationData":[OSD([subQ0]),TDD([makeQuery(id+"F0.imprint","IMPRINT",EDGE,{"disambiguationData":[TD([[makeQuery(id+"F0.imprint","INTERSECT",VERTEX,{"derivedFrom":[subQ0,sQuery(id+"F0.wireOp",EDGE,"E23.0")]}),-1.0]])],"derivedFrom":subQ0})])],"isStart":false});}
            var Q46;
            {var subQ0=sQuery(id+"F0.wireOp",EDGE,"E11.0");Q46=makeQuery(id+"F1.opExtrude","CAP_EDGE",EDGE,{"disambiguationData":[OSD([subQ0]),TDD([makeQuery(id+"F0.imprint","IMPRINT",EDGE,{"disambiguationData":[TD([[makeQuery(id+"F0.imprint","INTERSECT",VERTEX,{"derivedFrom":[subQ0,sQuery(id+"F0.wireOp",EDGE,"E23.0")]}),-1.0]])],"derivedFrom":subQ0})])],"isStart":false});}
            var Q47;
            {var subQ0=sQuery(id+"F0.wireOp",EDGE,"E9.0");Q47=makeQuery(id+"F1.opExtrude","CAP_EDGE",EDGE,{"disambiguationData":[OSD([subQ0]),TDD([makeQuery(id+"F0.imprint","IMPRINT",EDGE,{"disambiguationData":[TD([[makeQuery(id+"F0.imprint","INTERSECT",VERTEX,{"derivedFrom":[subQ0,sQuery(id+"F0.wireOp",EDGE,"E21.0")]}),-1.0]])],"derivedFrom":subQ0})])],"isStart":false});}
            var Q48;
            {var subQ0=sQuery(id+"F0.wireOp",EDGE,"E11.0");Q48=makeQuery(id+"F1.opExtrude","CAP_EDGE",EDGE,{"disambiguationData":[OSD([subQ0]),TDD([makeQuery(id+"F0.imprint","IMPRINT",EDGE,{"disambiguationData":[TD([[makeQuery(id+"F0.imprint","INTERSECT",VERTEX,{"derivedFrom":[subQ0,sQuery(id+"F0.wireOp",EDGE,"E21.0")]}),-1.0]])],"derivedFrom":subQ0})])],"isStart":false});}
            var Q49;
            {var subQ0=sQuery(id+"F0.wireOp",EDGE,"E9.0");Q49=makeQuery(id+"F1.opExtrude","CAP_EDGE",EDGE,{"disambiguationData":[OSD([subQ0]),TDD([makeQuery(id+"F0.imprint","IMPRINT",EDGE,{"disambiguationData":[TD([[makeQuery(id+"F0.imprint","INTERSECT",VERTEX,{"derivedFrom":[subQ0,sQuery(id+"F0.wireOp",EDGE,"E19.0")]}),-1.0]])],"derivedFrom":subQ0})])],"isStart":false});}
            var Q50;
            {var subQ0=sQuery(id+"F0.wireOp",EDGE,"E11.0");Q50=makeQuery(id+"F1.opExtrude","CAP_EDGE",EDGE,{"disambiguationData":[OSD([subQ0]),TDD([makeQuery(id+"F0.imprint","IMPRINT",EDGE,{"disambiguationData":[TD([[makeQuery(id+"F0.imprint","INTERSECT",VERTEX,{"derivedFrom":[subQ0,sQuery(id+"F0.wireOp",EDGE,"E19.0")]}),-1.0]])],"derivedFrom":subQ0})])],"isStart":false});}
            var Q51;
            {var subQ0=sQuery(id+"F0.wireOp",EDGE,"E9.0");Q51=makeQuery(id+"F1.opExtrude","CAP_EDGE",EDGE,{"disambiguationData":[OSD([subQ0]),TDD([makeQuery(id+"F0.imprint","IMPRINT",EDGE,{"disambiguationData":[TD([[makeQuery(id+"F0.imprint","INTERSECT",VERTEX,{"derivedFrom":[subQ0,sQuery(id+"F0.wireOp",EDGE,"E17.0")]}),-1.0]])],"derivedFrom":subQ0})])],"isStart":false});}
            var Q52;
            {var subQ0=sQuery(id+"F0.wireOp",EDGE,"E11.0");Q52=makeQuery(id+"F1.opExtrude","CAP_EDGE",EDGE,{"disambiguationData":[OSD([subQ0]),TDD([makeQuery(id+"F0.imprint","IMPRINT",EDGE,{"disambiguationData":[TD([[makeQuery(id+"F0.imprint","INTERSECT",VERTEX,{"derivedFrom":[subQ0,sQuery(id+"F0.wireOp",EDGE,"E17.0")]}),-1.0]])],"derivedFrom":subQ0})])],"isStart":false});}
            var Q53;
            {var subQ0=sQuery(id+"F0.wireOp",EDGE,"E9.0");Q53=makeQuery(id+"F1.opExtrude","CAP_EDGE",EDGE,{"disambiguationData":[OSD([subQ0]),TDD([makeQuery(id+"F0.imprint","IMPRINT",EDGE,{"disambiguationData":[TD([[makeQuery(id+"F0.imprint","INTERSECT",VERTEX,{"derivedFrom":[subQ0,sQuery(id+"F0.wireOp",EDGE,"E15.0")]}),-1.0]])],"derivedFrom":subQ0})])],"isStart":false});}
            var Q54;
            {var subQ0=sQuery(id+"F0.wireOp",EDGE,"E11.0");Q54=makeQuery(id+"F1.opExtrude","CAP_EDGE",EDGE,{"disambiguationData":[OSD([subQ0]),TDD([makeQuery(id+"F0.imprint","IMPRINT",EDGE,{"disambiguationData":[TD([[makeQuery(id+"F0.imprint","INTERSECT",VERTEX,{"derivedFrom":[subQ0,sQuery(id+"F0.wireOp",EDGE,"E15.0")]}),-1.0]])],"derivedFrom":subQ0})])],"isStart":false});}
            var Q55;
            {var subQ0=sQuery(id+"F0.wireOp",EDGE,"E13.0");Q55=makeQuery(id+"F1.opExtrude","CAP_EDGE",EDGE,{"disambiguationData":[OSD([subQ0]),TDD([makeQuery(id+"F0.imprint","IMPRINT",EDGE,{"disambiguationData":[TD([[makeQuery(id+"F0.imprint","INTERSECT",VERTEX,{"derivedFrom":[subQ0,sQuery(id+"F0.wireOp",EDGE,"E17.0")]}),-1.0]])],"derivedFrom":subQ0})])],"isStart":false});}
            var Q56;
            {var subQ0=sQuery(id+"F0.wireOp",EDGE,"E12.0");Q56=makeQuery(id+"F1.opExtrude","CAP_EDGE",EDGE,{"disambiguationData":[OSD([subQ0]),TDD([makeQuery(id+"F0.imprint","IMPRINT",EDGE,{"disambiguationData":[TD([[makeQuery(id+"F0.imprint","INTERSECT",VERTEX,{"derivedFrom":[subQ0,sQuery(id+"F0.wireOp",EDGE,"E17.0")]}),-1.0]])],"derivedFrom":subQ0})])],"isStart":false});}
            var Q57;
            {var subQ0=sQuery(id+"F0.wireOp",EDGE,"E13.0");Q57=makeQuery(id+"F1.opExtrude","CAP_EDGE",EDGE,{"disambiguationData":[OSD([subQ0]),TDD([makeQuery(id+"F0.imprint","IMPRINT",EDGE,{"disambiguationData":[TD([[makeQuery(id+"F0.imprint","INTERSECT",VERTEX,{"derivedFrom":[subQ0,sQuery(id+"F0.wireOp",EDGE,"E15.0")]}),-1.0]])],"derivedFrom":subQ0})])],"isStart":false});}
            var Q58;
            {var subQ0=sQuery(id+"F0.wireOp",EDGE,"E12.0");Q58=makeQuery(id+"F1.opExtrude","CAP_EDGE",EDGE,{"disambiguationData":[OSD([subQ0]),TDD([makeQuery(id+"F0.imprint","IMPRINT",EDGE,{"disambiguationData":[TD([[makeQuery(id+"F0.imprint","INTERSECT",VERTEX,{"derivedFrom":[subQ0,sQuery(id+"F0.wireOp",EDGE,"E15.0")]}),-1.0]])],"derivedFrom":subQ0})])],"isStart":false});}
            var Q59;
            {var subQ0=sQuery(id+"F0.wireOp",EDGE,"E10.0");Q59=makeQuery(id+"F1.opExtrude","CAP_EDGE",EDGE,{"disambiguationData":[OSD([subQ0]),TDD([makeQuery(id+"F0.imprint","IMPRINT",EDGE,{"disambiguationData":[TD([[makeQuery(id+"F0.imprint","INTERSECT",VERTEX,{"derivedFrom":[subQ0,sQuery(id+"F0.wireOp",EDGE,"E15.0")]}),-1.0]])],"derivedFrom":subQ0})])],"isStart":false});}
            var Q60;
            {var subQ0=sQuery(id+"F0.wireOp",EDGE,"E8.0");Q60=makeQuery(id+"F1.opExtrude","CAP_EDGE",EDGE,{"disambiguationData":[OSD([subQ0]),TDD([makeQuery(id+"F0.imprint","IMPRINT",EDGE,{"disambiguationData":[TD([[makeQuery(id+"F0.imprint","INTERSECT",VERTEX,{"derivedFrom":[subQ0,sQuery(id+"F0.wireOp",EDGE,"E15.0")]}),-1.0]])],"derivedFrom":subQ0})])],"isStart":false});}
            fillet(context, id + "F2", {"entities" : qUnion([Q0, Q1, Q2, Q3, Q4, Q5, Q6, Q7, Q8, Q9, Q10, Q11, Q12, Q13, Q14, Q15, Q16, Q17, Q18, Q19, Q20, Q21, Q22, Q23, Q24, Q25, Q26, Q27, Q28, Q29, Q30, Q31, Q32, Q33, Q34, Q35, Q36, Q37, Q38, Q39, Q40, Q41, Q42, Q43, Q44, Q45, Q46, Q47, Q48, Q49, Q50, Q51, Q52, Q53, Q54, Q55, Q56, Q57, Q58, Q59, Q60]), "radius" : .6 * mm, "tangentPropagation" : true, "allowEdgeOverflow" : false});
        }
        {
            var Q0;
            {var subQ0=sQuery(id+"F0.wireOp",EDGE,"85c74178-88a3-4eaf-b492-32c6037f9e62.0");Q0=makeQuery(id+"F1.opExtrude","CAP_EDGE",EDGE,{"disambiguationData":[OSD([subQ0]),TDD([makeQuery(id+"F0.imprint","IMPRINT",EDGE,{"disambiguationData":[TD([[makeQuery(id+"F0.imprint","INTERSECT",VERTEX,{"derivedFrom":[sQuery(id+"F0.wireOp",EDGE,"3e5cf576-49dc-4465-ad3e-ca1242db3cf5.0"),subQ0]}),-1.0]])],"derivedFrom":subQ0})])],"isStart":false});}
            var Q1;
            {var subQ0=sQuery(id+"F0.wireOp",EDGE,"3e5cf576-49dc-4465-ad3e-ca1242db3cf5.0");Q1=makeQuery(id+"F1.opExtrude","CAP_EDGE",EDGE,{"disambiguationData":[OSD([subQ0]),TDD([makeQuery(id+"F0.imprint","IMPRINT",EDGE,{"disambiguationData":[TD([[makeQuery(id+"F0.imprint","INTERSECT",VERTEX,{"derivedFrom":[subQ0,sQuery(id+"F0.wireOp",EDGE,"85c74178-88a3-4eaf-b492-32c6037f9e62.0")]}),-1.0]])],"derivedFrom":subQ0})])],"isStart":false});}
            var Q2;
            {var subQ0=sQuery(id+"F0.wireOp",EDGE,"b2fe94c1-cc08-47c4-b663-ca396442125b.0");Q2=makeQuery(id+"F1.opExtrude","CAP_EDGE",EDGE,{"disambiguationData":[OSD([subQ0]),TDD([makeQuery(id+"F0.imprint","IMPRINT",EDGE,{"disambiguationData":[TD([[makeQuery(id+"F0.imprint","INTERSECT",VERTEX,{"derivedFrom":[subQ0,sQuery(id+"F0.wireOp",EDGE,"85c74178-88a3-4eaf-b492-32c6037f9e62.0")]}),-1.0]])],"derivedFrom":subQ0})])],"isStart":false});}
            var Q3;
            {var subQ0=sQuery(id+"F0.wireOp",EDGE,"9343b0c3-cd2f-487d-bd13-aee8d7f259e0.0");Q3=makeQuery(id+"F1.opExtrude","CAP_EDGE",EDGE,{"disambiguationData":[OSD([subQ0]),TDD([makeQuery(id+"F0.imprint","IMPRINT",EDGE,{"disambiguationData":[TD([[makeQuery(id+"F0.imprint","INTERSECT",VERTEX,{"derivedFrom":[subQ0,sQuery(id+"F0.wireOp",EDGE,"85c74178-88a3-4eaf-b492-32c6037f9e62.0")]}),-1.0]])],"derivedFrom":subQ0})])],"isStart":false});}
            var Q4;
            {var subQ0=sQuery(id+"F0.wireOp",EDGE,"85c74178-88a3-4eaf-b492-32c6037f9e62.0");Q4=makeQuery(id+"F1.opExtrude","CAP_EDGE",EDGE,{"disambiguationData":[OSD([subQ0]),TDD([makeQuery(id+"F0.imprint","IMPRINT",EDGE,{"disambiguationData":[TD([[makeQuery(id+"F0.imprint","INTERSECT",VERTEX,{"derivedFrom":[sQuery(id+"F0.wireOp",EDGE,"9343b0c3-cd2f-487d-bd13-aee8d7f259e0.0"),subQ0]}),-1.0]])],"derivedFrom":subQ0})])],"isStart":false});}
            var Q5;
            {var subQ0=sQuery(id+"F0.wireOp",EDGE,"e2eb8f05-34aa-4610-8b14-5d7565173b4d.0");Q5=makeQuery(id+"F1.opExtrude","CAP_EDGE",EDGE,{"disambiguationData":[OSD([subQ0]),TDD([makeQuery(id+"F0.imprint","IMPRINT",EDGE,{"disambiguationData":[TD([[makeQuery(id+"F0.imprint","INTERSECT",VERTEX,{"derivedFrom":[subQ0,sQuery(id+"F0.wireOp",EDGE,"85c74178-88a3-4eaf-b492-32c6037f9e62.0")]}),-1.0]])],"derivedFrom":subQ0})])],"isStart":false});}
            var Q6;
            {var subQ0=sQuery(id+"F0.wireOp",EDGE,"23e37434-4ebb-4948-80c8-8d17bba51405.0");Q6=makeQuery(id+"F1.opExtrude","CAP_EDGE",EDGE,{"disambiguationData":[OSD([subQ0]),TDD([makeQuery(id+"F0.imprint","IMPRINT",EDGE,{"disambiguationData":[TD([[makeQuery(id+"F0.imprint","INTERSECT",VERTEX,{"derivedFrom":[subQ0,sQuery(id+"F0.wireOp",EDGE,"85c74178-88a3-4eaf-b492-32c6037f9e62.0")]}),-1.0]])],"derivedFrom":subQ0})])],"isStart":false});}
            var Q7;
            {var subQ0=sQuery(id+"F0.wireOp",EDGE,"bdac1eed-a409-4cee-9b7b-61454a391d7d.0");Q7=makeQuery(id+"F1.opExtrude","CAP_EDGE",EDGE,{"disambiguationData":[OSD([subQ0]),TDD([makeQuery(id+"F0.imprint","IMPRINT",EDGE,{"disambiguationData":[TD([[makeQuery(id+"F0.imprint","INTERSECT",VERTEX,{"derivedFrom":[subQ0,sQuery(id+"F0.wireOp",EDGE,"85c74178-88a3-4eaf-b492-32c6037f9e62.0")]}),-1.0]])],"derivedFrom":subQ0})])],"isStart":false});}
            var Q8;
            {var subQ0=sQuery(id+"F0.wireOp",EDGE,"f9003588-73a7-42be-b55c-edd191297de8.0");Q8=makeQuery(id+"F1.opExtrude","CAP_EDGE",EDGE,{"disambiguationData":[OSD([subQ0]),TDD([makeQuery(id+"F0.imprint","IMPRINT",EDGE,{"disambiguationData":[TD([[makeQuery(id+"F0.imprint","INTERSECT",VERTEX,{"derivedFrom":[subQ0,sQuery(id+"F0.wireOp",EDGE,"85c74178-88a3-4eaf-b492-32c6037f9e62.0")]}),-1.0]])],"derivedFrom":subQ0})])],"isStart":false});}
            var Q9;
            {var subQ0=sQuery(id+"F0.wireOp",EDGE,"a62689d6-4df4-411d-a8de-d30e4e7abbb4.0");Q9=makeQuery(id+"F1.opExtrude","CAP_EDGE",EDGE,{"disambiguationData":[OSD([subQ0]),TDD([makeQuery(id+"F0.imprint","IMPRINT",EDGE,{"disambiguationData":[TD([[makeQuery(id+"F0.imprint","INTERSECT",VERTEX,{"derivedFrom":[subQ0,sQuery(id+"F0.wireOp",EDGE,"85c74178-88a3-4eaf-b492-32c6037f9e62.0")]}),-1.0]])],"derivedFrom":subQ0})])],"isStart":false});}
            var Q10;
            {var subQ0=sQuery(id+"F0.wireOp",EDGE,"989afcd3-5a0d-4914-9734-28e95c678f40.0");Q10=makeQuery(id+"F1.opExtrude","CAP_EDGE",EDGE,{"disambiguationData":[OSD([subQ0]),TDD([makeQuery(id+"F0.imprint","IMPRINT",EDGE,{"disambiguationData":[TD([[makeQuery(id+"F0.imprint","INTERSECT",VERTEX,{"derivedFrom":[subQ0,sQuery(id+"F0.wireOp",EDGE,"450db5bc-e2e3-4f88-b9d5-953014a2ba1e.0")]}),-1.0]])],"derivedFrom":subQ0})])],"isStart":false});}
            var Q11;
            {var subQ0=sQuery(id+"F0.wireOp",EDGE,"85c74178-88a3-4eaf-b492-32c6037f9e62.0");Q11=makeQuery(id+"F1.opExtrude","CAP_EDGE",EDGE,{"disambiguationData":[OSD([subQ0]),TDD([makeQuery(id+"F0.imprint","IMPRINT",EDGE,{"disambiguationData":[TD([[makeQuery(id+"F0.imprint","INTERSECT",VERTEX,{"derivedFrom":[sQuery(id+"F0.wireOp",EDGE,"a62689d6-4df4-411d-a8de-d30e4e7abbb4.0"),subQ0]}),1.0]])],"derivedFrom":subQ0})])],"isStart":false});}
            var Q12;
            {var subQ0=sQuery(id+"F0.wireOp",EDGE,"85c74178-88a3-4eaf-b492-32c6037f9e62.0");Q12=makeQuery(id+"F1.opExtrude","CAP_EDGE",EDGE,{"disambiguationData":[OSD([subQ0]),TDD([makeQuery(id+"F0.imprint","IMPRINT",EDGE,{"disambiguationData":[TD([[makeQuery(id+"F0.imprint","INTERSECT",VERTEX,{"derivedFrom":[sQuery(id+"F0.wireOp",EDGE,"bdac1eed-a409-4cee-9b7b-61454a391d7d.0"),subQ0]}),1.0]])],"derivedFrom":subQ0})])],"isStart":false});}
            var Q13;
            {var subQ0=sQuery(id+"F0.wireOp",EDGE,"85c74178-88a3-4eaf-b492-32c6037f9e62.0");Q13=makeQuery(id+"F1.opExtrude","CAP_EDGE",EDGE,{"disambiguationData":[OSD([subQ0]),TDD([makeQuery(id+"F0.imprint","IMPRINT",EDGE,{"disambiguationData":[TD([[makeQuery(id+"F0.imprint","INTERSECT",VERTEX,{"derivedFrom":[sQuery(id+"F0.wireOp",EDGE,"862523a1-1db9-4ec9-a786-b55df2c1a98e.0"),subQ0]}),1.0]])],"derivedFrom":subQ0})])],"isStart":false});}
            var Q14;
            {var subQ0=sQuery(id+"F0.wireOp",EDGE,"862523a1-1db9-4ec9-a786-b55df2c1a98e.0");Q14=makeQuery(id+"F1.opExtrude","CAP_EDGE",EDGE,{"disambiguationData":[OSD([subQ0]),TDD([makeQuery(id+"F0.imprint","IMPRINT",EDGE,{"disambiguationData":[TD([[makeQuery(id+"F0.imprint","INTERSECT",VERTEX,{"derivedFrom":[subQ0,sQuery(id+"F0.wireOp",EDGE,"85c74178-88a3-4eaf-b492-32c6037f9e62.0")]}),-1.0]])],"derivedFrom":subQ0})])],"isStart":false});}
            var Q15;
            {var subQ0=sQuery(id+"F0.wireOp",EDGE,"854f07df-45a9-419d-971c-554534df12f4.0");Q15=makeQuery(id+"F1.opExtrude","CAP_EDGE",EDGE,{"disambiguationData":[OSD([subQ0]),TDD([makeQuery(id+"F0.imprint","IMPRINT",EDGE,{"disambiguationData":[TD([[makeQuery(id+"F0.imprint","INTERSECT",VERTEX,{"derivedFrom":[sQuery(id+"F0.wireOp",EDGE,"862523a1-1db9-4ec9-a786-b55df2c1a98e.0"),subQ0]}),1.0]])],"derivedFrom":subQ0})])],"isStart":false});}
            var Q16;
            {var subQ0=sQuery(id+"F0.wireOp",EDGE,"854f07df-45a9-419d-971c-554534df12f4.0");Q16=makeQuery(id+"F1.opExtrude","CAP_EDGE",EDGE,{"disambiguationData":[OSD([subQ0]),TDD([makeQuery(id+"F0.imprint","IMPRINT",EDGE,{"disambiguationData":[TD([[makeQuery(id+"F0.imprint","INTERSECT",VERTEX,{"derivedFrom":[sQuery(id+"F0.wireOp",EDGE,"a62689d6-4df4-411d-a8de-d30e4e7abbb4.0"),subQ0]}),1.0]])],"derivedFrom":subQ0})])],"isStart":false});}
            var Q17;
            {var subQ0=sQuery(id+"F0.wireOp",EDGE,"854f07df-45a9-419d-971c-554534df12f4.0");Q17=makeQuery(id+"F1.opExtrude","CAP_EDGE",EDGE,{"disambiguationData":[OSD([subQ0]),TDD([makeQuery(id+"F0.imprint","IMPRINT",EDGE,{"disambiguationData":[TD([[makeQuery(id+"F0.imprint","INTERSECT",VERTEX,{"derivedFrom":[sQuery(id+"F0.wireOp",EDGE,"bdac1eed-a409-4cee-9b7b-61454a391d7d.0"),subQ0]}),1.0]])],"derivedFrom":subQ0})])],"isStart":false});}
            var Q18;
            {var subQ0=sQuery(id+"F0.wireOp",EDGE,"854f07df-45a9-419d-971c-554534df12f4.0");Q18=makeQuery(id+"F1.opExtrude","CAP_EDGE",EDGE,{"disambiguationData":[OSD([subQ0]),TDD([makeQuery(id+"F0.imprint","IMPRINT",EDGE,{"disambiguationData":[TD([[makeQuery(id+"F0.imprint","INTERSECT",VERTEX,{"derivedFrom":[sQuery(id+"F0.wireOp",EDGE,"e2eb8f05-34aa-4610-8b14-5d7565173b4d.0"),subQ0]}),1.0]])],"derivedFrom":subQ0})])],"isStart":false});}
            var Q19;
            {var subQ0=sQuery(id+"F0.wireOp",EDGE,"854f07df-45a9-419d-971c-554534df12f4.0");Q19=makeQuery(id+"F1.opExtrude","CAP_EDGE",EDGE,{"disambiguationData":[OSD([subQ0]),TDD([makeQuery(id+"F0.imprint","IMPRINT",EDGE,{"disambiguationData":[TD([[makeQuery(id+"F0.imprint","INTERSECT",VERTEX,{"derivedFrom":[sQuery(id+"F0.wireOp",EDGE,"3e5cf576-49dc-4465-ad3e-ca1242db3cf5.0"),subQ0]}),-1.0]])],"derivedFrom":subQ0})])],"isStart":false});}
            var Q20;
            {var subQ0=sQuery(id+"F0.wireOp",EDGE,"E21.0");Q20=makeQuery(id+"F1.opExtrude","CAP_EDGE",EDGE,{"disambiguationData":[OSD([subQ0]),TDD([makeQuery(id+"F0.imprint","IMPRINT",EDGE,{"disambiguationData":[TD([[makeQuery(id+"F0.imprint","INTERSECT",VERTEX,{"derivedFrom":[sQuery(id+"F0.wireOp",EDGE,"E6.0"),subQ0]}),-1.0]])],"derivedFrom":subQ0})])],"isStart":false});}
            var Q21;
            {var subQ0=sQuery(id+"F0.wireOp",EDGE,"E22.0");Q21=makeQuery(id+"F1.opExtrude","CAP_EDGE",EDGE,{"disambiguationData":[OSD([subQ0]),TDD([makeQuery(id+"F0.imprint","IMPRINT",EDGE,{"disambiguationData":[TD([[makeQuery(id+"F0.imprint","INTERSECT",VERTEX,{"derivedFrom":[sQuery(id+"F0.wireOp",EDGE,"E6.0"),subQ0]}),-1.0]])],"derivedFrom":subQ0})])],"isStart":false});}
            var Q22;
            {var subQ0=sQuery(id+"F0.wireOp",EDGE,"E20.0");Q22=makeQuery(id+"F1.opExtrude","CAP_EDGE",EDGE,{"disambiguationData":[OSD([subQ0]),TDD([makeQuery(id+"F0.imprint","IMPRINT",EDGE,{"disambiguationData":[TD([[makeQuery(id+"F0.imprint","INTERSECT",VERTEX,{"derivedFrom":[sQuery(id+"F0.wireOp",EDGE,"E6.0"),subQ0]}),-1.0]])],"derivedFrom":subQ0})])],"isStart":false});}
            var Q23;
            {var subQ0=sQuery(id+"F0.wireOp",EDGE,"E18.0");Q23=makeQuery(id+"F1.opExtrude","CAP_EDGE",EDGE,{"disambiguationData":[OSD([subQ0]),TDD([makeQuery(id+"F0.imprint","IMPRINT",EDGE,{"disambiguationData":[TD([[makeQuery(id+"F0.imprint","INTERSECT",VERTEX,{"derivedFrom":[sQuery(id+"F0.wireOp",EDGE,"E6.0"),subQ0]}),-1.0]])],"derivedFrom":subQ0})])],"isStart":false});}
            var Q24;
            {var subQ0=sQuery(id+"F0.wireOp",EDGE,"E17.0");Q24=makeQuery(id+"F1.opExtrude","CAP_EDGE",EDGE,{"disambiguationData":[OSD([subQ0]),TDD([makeQuery(id+"F0.imprint","IMPRINT",EDGE,{"disambiguationData":[TD([[makeQuery(id+"F0.imprint","INTERSECT",VERTEX,{"derivedFrom":[sQuery(id+"F0.wireOp",EDGE,"E6.0"),subQ0]}),-1.0]])],"derivedFrom":subQ0})])],"isStart":false});}
            var Q25;
            {var subQ0=sQuery(id+"F0.wireOp",EDGE,"E6.0");Q25=makeQuery(id+"F1.opExtrude","CAP_EDGE",EDGE,{"disambiguationData":[OSD([subQ0]),TDD([makeQuery(id+"F0.imprint","IMPRINT",EDGE,{"disambiguationData":[TD([[makeQuery(id+"F0.imprint","INTERSECT",VERTEX,{"derivedFrom":[subQ0,sQuery(id+"F0.wireOp",EDGE,"E17.0")]}),-1.0]])],"derivedFrom":subQ0})])],"isStart":false});}
            var Q26;
            {var subQ0=sQuery(id+"F0.wireOp",EDGE,"E6.0");Q26=makeQuery(id+"F1.opExtrude","CAP_EDGE",EDGE,{"disambiguationData":[OSD([subQ0]),TDD([makeQuery(id+"F0.imprint","IMPRINT",EDGE,{"disambiguationData":[TD([[makeQuery(id+"F0.imprint","INTERSECT",VERTEX,{"derivedFrom":[subQ0,sQuery(id+"F0.wireOp",EDGE,"E19.0")]}),-1.0]])],"derivedFrom":subQ0})])],"isStart":false});}
            var Q27;
            {var subQ0=sQuery(id+"F0.wireOp",EDGE,"E6.0");Q27=makeQuery(id+"F1.opExtrude","CAP_EDGE",EDGE,{"disambiguationData":[OSD([subQ0]),TDD([makeQuery(id+"F0.imprint","IMPRINT",EDGE,{"disambiguationData":[TD([[makeQuery(id+"F0.imprint","INTERSECT",VERTEX,{"derivedFrom":[subQ0,sQuery(id+"F0.wireOp",EDGE,"E15.0")]}),-1.0]])],"derivedFrom":subQ0})])],"isStart":false});}
            var Q28;
            {var subQ0=sQuery(id+"F0.wireOp",EDGE,"E15.0");Q28=makeQuery(id+"F1.opExtrude","CAP_EDGE",EDGE,{"disambiguationData":[OSD([subQ0]),TDD([makeQuery(id+"F0.imprint","IMPRINT",EDGE,{"disambiguationData":[TD([[makeQuery(id+"F0.imprint","INTERSECT",VERTEX,{"derivedFrom":[sQuery(id+"F0.wireOp",EDGE,"E6.0"),subQ0]}),-1.0]])],"derivedFrom":subQ0})])],"isStart":false});}
            var Q29;
            {var subQ0=sQuery(id+"F0.wireOp",EDGE,"E16.0");Q29=makeQuery(id+"F1.opExtrude","CAP_EDGE",EDGE,{"disambiguationData":[OSD([subQ0]),TDD([makeQuery(id+"F0.imprint","IMPRINT",EDGE,{"disambiguationData":[TD([[makeQuery(id+"F0.imprint","INTERSECT",VERTEX,{"derivedFrom":[sQuery(id+"F0.wireOp",EDGE,"E6.0"),subQ0]}),-1.0]])],"derivedFrom":subQ0})])],"isStart":false});}
            var Q30;
            {var subQ0=sQuery(id+"F0.wireOp",EDGE,"E14.0");Q30=makeQuery(id+"F1.opExtrude","CAP_EDGE",EDGE,{"disambiguationData":[OSD([subQ0]),TDD([makeQuery(id+"F0.imprint","IMPRINT",EDGE,{"disambiguationData":[TD([[makeQuery(id+"F0.imprint","INTERSECT",VERTEX,{"derivedFrom":[sQuery(id+"F0.wireOp",EDGE,"E6.0"),subQ0]}),-1.0]])],"derivedFrom":subQ0})])],"isStart":false});}
            var Q31;
            {var subQ0=sQuery(id+"F0.wireOp",EDGE,"E14.0");Q31=makeQuery(id+"F1.opExtrude","CAP_EDGE",EDGE,{"disambiguationData":[OSD([subQ0]),TDD([makeQuery(id+"F0.imprint","IMPRINT",EDGE,{"disambiguationData":[TD([[makeQuery(id+"F0.imprint","INTERSECT",VERTEX,{"derivedFrom":[sQuery(id+"F0.wireOp",EDGE,"E10.0"),subQ0]}),-1.0]])],"derivedFrom":subQ0})])],"isStart":false});}
            var Q32;
            {var subQ0=sQuery(id+"F0.wireOp",EDGE,"E15.0");Q32=makeQuery(id+"F1.opExtrude","CAP_EDGE",EDGE,{"disambiguationData":[OSD([subQ0]),TDD([makeQuery(id+"F0.imprint","IMPRINT",EDGE,{"disambiguationData":[TD([[makeQuery(id+"F0.imprint","INTERSECT",VERTEX,{"derivedFrom":[sQuery(id+"F0.wireOp",EDGE,"E10.0"),subQ0]}),-1.0]])],"derivedFrom":subQ0})])],"isStart":false});}
            var Q33;
            {var subQ0=sQuery(id+"F0.wireOp",EDGE,"E16.0");Q33=makeQuery(id+"F1.opExtrude","CAP_EDGE",EDGE,{"disambiguationData":[OSD([subQ0]),TDD([makeQuery(id+"F0.imprint","IMPRINT",EDGE,{"disambiguationData":[TD([[makeQuery(id+"F0.imprint","INTERSECT",VERTEX,{"derivedFrom":[sQuery(id+"F0.wireOp",EDGE,"E10.0"),subQ0]}),-1.0]])],"derivedFrom":subQ0})])],"isStart":false});}
            var Q34;
            {var subQ0=sQuery(id+"F0.wireOp",EDGE,"E16.0");Q34=makeQuery(id+"F1.opExtrude","CAP_EDGE",EDGE,{"disambiguationData":[OSD([subQ0]),TDD([makeQuery(id+"F0.imprint","IMPRINT",EDGE,{"disambiguationData":[TD([[makeQuery(id+"F0.imprint","INTERSECT",VERTEX,{"derivedFrom":[sQuery(id+"F0.wireOp",EDGE,"E11.0"),subQ0]}),1.0]])],"derivedFrom":subQ0})])],"isStart":false});}
            var Q35;
            {var subQ0=sQuery(id+"F0.wireOp",EDGE,"E15.0");Q35=makeQuery(id+"F1.opExtrude","CAP_EDGE",EDGE,{"disambiguationData":[OSD([subQ0]),TDD([makeQuery(id+"F0.imprint","IMPRINT",EDGE,{"disambiguationData":[TD([[makeQuery(id+"F0.imprint","INTERSECT",VERTEX,{"derivedFrom":[sQuery(id+"F0.wireOp",EDGE,"E11.0"),subQ0]}),1.0]])],"derivedFrom":subQ0})])],"isStart":false});}
            var Q36;
            {var subQ0=sQuery(id+"F0.wireOp",EDGE,"E14.0");Q36=makeQuery(id+"F1.opExtrude","CAP_EDGE",EDGE,{"disambiguationData":[OSD([subQ0]),TDD([makeQuery(id+"F0.imprint","IMPRINT",EDGE,{"disambiguationData":[TD([[makeQuery(id+"F0.imprint","INTERSECT",VERTEX,{"derivedFrom":[sQuery(id+"F0.wireOp",EDGE,"E11.0"),subQ0]}),1.0]])],"derivedFrom":subQ0})])],"isStart":false});}
            var Q37;
            {var subQ0=sQuery(id+"F0.wireOp",EDGE,"E14.0");Q37=makeQuery(id+"F1.opExtrude","CAP_EDGE",EDGE,{"disambiguationData":[OSD([subQ0]),TDD([makeQuery(id+"F0.imprint","IMPRINT",EDGE,{"disambiguationData":[TD([[makeQuery(id+"F0.imprint","INTERSECT",VERTEX,{"derivedFrom":[sQuery(id+"F0.wireOp",EDGE,"E7.0"),subQ0]}),1.0]])],"derivedFrom":subQ0})])],"isStart":false});}
            var Q38;
            {var subQ0=sQuery(id+"F0.wireOp",EDGE,"E7.0");Q38=makeQuery(id+"F1.opExtrude","CAP_EDGE",EDGE,{"disambiguationData":[OSD([subQ0]),TDD([makeQuery(id+"F0.imprint","IMPRINT",EDGE,{"disambiguationData":[TD([[makeQuery(id+"F0.imprint","INTERSECT",VERTEX,{"derivedFrom":[subQ0,sQuery(id+"F0.wireOp",EDGE,"E15.0")]}),-1.0]])],"derivedFrom":subQ0})])],"isStart":false});}
            var Q39;
            {var subQ0=sQuery(id+"F0.wireOp",EDGE,"E15.0");Q39=makeQuery(id+"F1.opExtrude","CAP_EDGE",EDGE,{"disambiguationData":[OSD([subQ0]),TDD([makeQuery(id+"F0.imprint","IMPRINT",EDGE,{"disambiguationData":[TD([[makeQuery(id+"F0.imprint","INTERSECT",VERTEX,{"derivedFrom":[sQuery(id+"F0.wireOp",EDGE,"E7.0"),subQ0]}),1.0]])],"derivedFrom":subQ0})])],"isStart":false});}
            var Q40;
            {var subQ0=sQuery(id+"F0.wireOp",EDGE,"E16.0");Q40=makeQuery(id+"F1.opExtrude","CAP_EDGE",EDGE,{"disambiguationData":[OSD([subQ0]),TDD([makeQuery(id+"F0.imprint","IMPRINT",EDGE,{"disambiguationData":[TD([[makeQuery(id+"F0.imprint","INTERSECT",VERTEX,{"derivedFrom":[sQuery(id+"F0.wireOp",EDGE,"E7.0"),subQ0]}),1.0]])],"derivedFrom":subQ0})])],"isStart":false});}
            var Q41;
            {var subQ0=sQuery(id+"F0.wireOp",EDGE,"E7.0");Q41=makeQuery(id+"F1.opExtrude","CAP_EDGE",EDGE,{"disambiguationData":[OSD([subQ0]),TDD([makeQuery(id+"F0.imprint","IMPRINT",EDGE,{"disambiguationData":[TD([[makeQuery(id+"F0.imprint","INTERSECT",VERTEX,{"derivedFrom":[subQ0,sQuery(id+"F0.wireOp",EDGE,"E17.0")]}),-1.0]])],"derivedFrom":subQ0})])],"isStart":false});}
            var Q42;
            {var subQ0=sQuery(id+"F0.wireOp",EDGE,"E17.0");Q42=makeQuery(id+"F1.opExtrude","CAP_EDGE",EDGE,{"disambiguationData":[OSD([subQ0]),TDD([makeQuery(id+"F0.imprint","IMPRINT",EDGE,{"disambiguationData":[TD([[makeQuery(id+"F0.imprint","INTERSECT",VERTEX,{"derivedFrom":[sQuery(id+"F0.wireOp",EDGE,"E7.0"),subQ0]}),1.0]])],"derivedFrom":subQ0})])],"isStart":false});}
            var Q43;
            {var subQ0=sQuery(id+"F0.wireOp",EDGE,"E18.0");Q43=makeQuery(id+"F1.opExtrude","CAP_EDGE",EDGE,{"disambiguationData":[OSD([subQ0]),TDD([makeQuery(id+"F0.imprint","IMPRINT",EDGE,{"disambiguationData":[TD([[makeQuery(id+"F0.imprint","INTERSECT",VERTEX,{"derivedFrom":[sQuery(id+"F0.wireOp",EDGE,"E7.0"),subQ0]}),1.0]])],"derivedFrom":subQ0})])],"isStart":false});}
            var Q44;
            {var subQ0=sQuery(id+"F0.wireOp",EDGE,"E17.0");Q44=makeQuery(id+"F1.opExtrude","CAP_EDGE",EDGE,{"disambiguationData":[OSD([subQ0]),TDD([makeQuery(id+"F0.imprint","IMPRINT",EDGE,{"disambiguationData":[TD([[makeQuery(id+"F0.imprint","INTERSECT",VERTEX,{"derivedFrom":[sQuery(id+"F0.wireOp",EDGE,"E11.0"),subQ0]}),1.0]])],"derivedFrom":subQ0})])],"isStart":false});}
            var Q45;
            {var subQ0=sQuery(id+"F0.wireOp",EDGE,"E18.0");Q45=makeQuery(id+"F1.opExtrude","CAP_EDGE",EDGE,{"disambiguationData":[OSD([subQ0]),TDD([makeQuery(id+"F0.imprint","IMPRINT",EDGE,{"disambiguationData":[TD([[makeQuery(id+"F0.imprint","INTERSECT",VERTEX,{"derivedFrom":[sQuery(id+"F0.wireOp",EDGE,"E11.0"),subQ0]}),1.0]])],"derivedFrom":subQ0})])],"isStart":false});}
            var Q46;
            {var subQ0=sQuery(id+"F0.wireOp",EDGE,"E18.0");Q46=makeQuery(id+"F1.opExtrude","CAP_EDGE",EDGE,{"disambiguationData":[OSD([subQ0]),TDD([makeQuery(id+"F0.imprint","IMPRINT",EDGE,{"disambiguationData":[TD([[makeQuery(id+"F0.imprint","INTERSECT",VERTEX,{"derivedFrom":[sQuery(id+"F0.wireOp",EDGE,"E10.0"),subQ0]}),-1.0]])],"derivedFrom":subQ0})])],"isStart":false});}
            var Q47;
            {var subQ0=sQuery(id+"F0.wireOp",EDGE,"E17.0");Q47=makeQuery(id+"F1.opExtrude","CAP_EDGE",EDGE,{"disambiguationData":[OSD([subQ0]),TDD([makeQuery(id+"F0.imprint","IMPRINT",EDGE,{"disambiguationData":[TD([[makeQuery(id+"F0.imprint","INTERSECT",VERTEX,{"derivedFrom":[sQuery(id+"F0.wireOp",EDGE,"E10.0"),subQ0]}),-1.0]])],"derivedFrom":subQ0})])],"isStart":false});}
            var Q48;
            {var subQ0=sQuery(id+"F0.wireOp",EDGE,"E7.0");Q48=makeQuery(id+"F1.opExtrude","CAP_EDGE",EDGE,{"disambiguationData":[OSD([subQ0]),TDD([makeQuery(id+"F0.imprint","IMPRINT",EDGE,{"disambiguationData":[TD([[makeQuery(id+"F0.imprint","INTERSECT",VERTEX,{"derivedFrom":[subQ0,sQuery(id+"F0.wireOp",EDGE,"E19.0")]}),-1.0]])],"derivedFrom":subQ0})])],"isStart":false});}
            var Q49;
            {var subQ0=sQuery(id+"F0.wireOp",EDGE,"E19.0");Q49=makeQuery(id+"F1.opExtrude","CAP_EDGE",EDGE,{"disambiguationData":[OSD([subQ0]),TDD([makeQuery(id+"F0.imprint","IMPRINT",EDGE,{"disambiguationData":[TD([[makeQuery(id+"F0.imprint","INTERSECT",VERTEX,{"derivedFrom":[sQuery(id+"F0.wireOp",EDGE,"E7.0"),subQ0]}),1.0]])],"derivedFrom":subQ0})])],"isStart":false});}
            var Q50;
            {var subQ0=sQuery(id+"F0.wireOp",EDGE,"E20.0");Q50=makeQuery(id+"F1.opExtrude","CAP_EDGE",EDGE,{"disambiguationData":[OSD([subQ0]),TDD([makeQuery(id+"F0.imprint","IMPRINT",EDGE,{"disambiguationData":[TD([[makeQuery(id+"F0.imprint","INTERSECT",VERTEX,{"derivedFrom":[sQuery(id+"F0.wireOp",EDGE,"E11.0"),subQ0]}),1.0]])],"derivedFrom":subQ0})])],"isStart":false});}
            var Q51;
            {var subQ0=sQuery(id+"F0.wireOp",EDGE,"E19.0");Q51=makeQuery(id+"F1.opExtrude","CAP_EDGE",EDGE,{"disambiguationData":[OSD([subQ0]),TDD([makeQuery(id+"F0.imprint","IMPRINT",EDGE,{"disambiguationData":[TD([[makeQuery(id+"F0.imprint","INTERSECT",VERTEX,{"derivedFrom":[sQuery(id+"F0.wireOp",EDGE,"E11.0"),subQ0]}),1.0]])],"derivedFrom":subQ0})])],"isStart":false});}
            var Q52;
            {var subQ0=sQuery(id+"F0.wireOp",EDGE,"E20.0");Q52=makeQuery(id+"F1.opExtrude","CAP_EDGE",EDGE,{"disambiguationData":[OSD([subQ0]),TDD([makeQuery(id+"F0.imprint","IMPRINT",EDGE,{"disambiguationData":[TD([[makeQuery(id+"F0.imprint","INTERSECT",VERTEX,{"derivedFrom":[sQuery(id+"F0.wireOp",EDGE,"E10.0"),subQ0]}),-1.0]])],"derivedFrom":subQ0})])],"isStart":false});}
            var Q53;
            {var subQ0=sQuery(id+"F0.wireOp",EDGE,"E19.0");Q53=makeQuery(id+"F1.opExtrude","CAP_EDGE",EDGE,{"disambiguationData":[OSD([subQ0]),TDD([makeQuery(id+"F0.imprint","IMPRINT",EDGE,{"disambiguationData":[TD([[makeQuery(id+"F0.imprint","INTERSECT",VERTEX,{"derivedFrom":[sQuery(id+"F0.wireOp",EDGE,"E10.0"),subQ0]}),-1.0]])],"derivedFrom":subQ0})])],"isStart":false});}
            var Q54;
            {var subQ0=sQuery(id+"F0.wireOp",EDGE,"E21.0");Q54=makeQuery(id+"F1.opExtrude","CAP_EDGE",EDGE,{"disambiguationData":[OSD([subQ0]),TDD([makeQuery(id+"F0.imprint","IMPRINT",EDGE,{"disambiguationData":[TD([[makeQuery(id+"F0.imprint","INTERSECT",VERTEX,{"derivedFrom":[sQuery(id+"F0.wireOp",EDGE,"E11.0"),subQ0]}),1.0]])],"derivedFrom":subQ0})])],"isStart":false});}
            var Q55;
            {var subQ0=sQuery(id+"F0.wireOp",EDGE,"E22.0");Q55=makeQuery(id+"F1.opExtrude","CAP_EDGE",EDGE,{"disambiguationData":[OSD([subQ0]),TDD([makeQuery(id+"F0.imprint","IMPRINT",EDGE,{"disambiguationData":[TD([[makeQuery(id+"F0.imprint","INTERSECT",VERTEX,{"derivedFrom":[sQuery(id+"F0.wireOp",EDGE,"E11.0"),subQ0]}),1.0]])],"derivedFrom":subQ0})])],"isStart":false});}
            var Q56;
            {var subQ0=sQuery(id+"F0.wireOp",EDGE,"E22.0");Q56=makeQuery(id+"F1.opExtrude","CAP_EDGE",EDGE,{"disambiguationData":[OSD([subQ0]),TDD([makeQuery(id+"F0.imprint","IMPRINT",EDGE,{"disambiguationData":[TD([[makeQuery(id+"F0.imprint","INTERSECT",VERTEX,{"derivedFrom":[sQuery(id+"F0.wireOp",EDGE,"E7.0"),subQ0]}),1.0]])],"derivedFrom":subQ0})])],"isStart":false});}
            var Q57;
            {var subQ0=sQuery(id+"F0.wireOp",EDGE,"E21.0");Q57=makeQuery(id+"F1.opExtrude","CAP_EDGE",EDGE,{"disambiguationData":[OSD([subQ0]),TDD([makeQuery(id+"F0.imprint","IMPRINT",EDGE,{"disambiguationData":[TD([[makeQuery(id+"F0.imprint","INTERSECT",VERTEX,{"derivedFrom":[sQuery(id+"F0.wireOp",EDGE,"E7.0"),subQ0]}),1.0]])],"derivedFrom":subQ0})])],"isStart":false});}
            var Q58;
            {var subQ0=sQuery(id+"F0.wireOp",EDGE,"E7.0");Q58=makeQuery(id+"F1.opExtrude","CAP_EDGE",EDGE,{"disambiguationData":[OSD([subQ0]),TDD([makeQuery(id+"F0.imprint","IMPRINT",EDGE,{"disambiguationData":[TD([[makeQuery(id+"F0.imprint","INTERSECT",VERTEX,{"derivedFrom":[subQ0,sQuery(id+"F0.wireOp",EDGE,"E21.0")]}),-1.0]])],"derivedFrom":subQ0})])],"isStart":false});}
            var Q59;
            {var subQ0=sQuery(id+"F0.wireOp",EDGE,"E7.0");Q59=makeQuery(id+"F1.opExtrude","CAP_EDGE",EDGE,{"disambiguationData":[OSD([subQ0]),TDD([makeQuery(id+"F0.imprint","IMPRINT",EDGE,{"disambiguationData":[TD([[makeQuery(id+"F0.imprint","INTERSECT",VERTEX,{"derivedFrom":[subQ0,sQuery(id+"F0.wireOp",EDGE,"E23.0")]}),-1.0]])],"derivedFrom":subQ0})])],"isStart":false});}
            var Q60;
            {var subQ0=sQuery(id+"F0.wireOp",EDGE,"E23.0");Q60=makeQuery(id+"F1.opExtrude","CAP_EDGE",EDGE,{"disambiguationData":[OSD([subQ0]),TDD([makeQuery(id+"F0.imprint","IMPRINT",EDGE,{"disambiguationData":[TD([[makeQuery(id+"F0.imprint","INTERSECT",VERTEX,{"derivedFrom":[sQuery(id+"F0.wireOp",EDGE,"E7.0"),subQ0]}),1.0]])],"derivedFrom":subQ0})])],"isStart":false});}
            var Q61;
            {var subQ0=sQuery(id+"F0.wireOp",EDGE,"E23.0");Q61=makeQuery(id+"F1.opExtrude","CAP_EDGE",EDGE,{"disambiguationData":[OSD([subQ0]),TDD([makeQuery(id+"F0.imprint","IMPRINT",EDGE,{"disambiguationData":[TD([[makeQuery(id+"F0.imprint","INTERSECT",VERTEX,{"derivedFrom":[sQuery(id+"F0.wireOp",EDGE,"E11.0"),subQ0]}),1.0]])],"derivedFrom":subQ0})])],"isStart":false});}
            var Q62;
            {var subQ0=sQuery(id+"F0.wireOp",EDGE,"E20.0");Q62=makeQuery(id+"F1.opExtrude","CAP_EDGE",EDGE,{"disambiguationData":[OSD([subQ0]),TDD([makeQuery(id+"F0.imprint","IMPRINT",EDGE,{"disambiguationData":[TD([[makeQuery(id+"F0.imprint","INTERSECT",VERTEX,{"derivedFrom":[sQuery(id+"F0.wireOp",EDGE,"E7.0"),subQ0]}),1.0]])],"derivedFrom":subQ0})])],"isStart":false});}
            var Q63;
            {var subQ0=sQuery(id+"F0.wireOp",EDGE,"E21.0");Q63=makeQuery(id+"F1.opExtrude","CAP_EDGE",EDGE,{"disambiguationData":[OSD([subQ0]),TDD([makeQuery(id+"F0.imprint","IMPRINT",EDGE,{"disambiguationData":[TD([[makeQuery(id+"F0.imprint","INTERSECT",VERTEX,{"derivedFrom":[sQuery(id+"F0.wireOp",EDGE,"E10.0"),subQ0]}),-1.0]])],"derivedFrom":subQ0})])],"isStart":false});}
            var Q64;
            {var subQ0=sQuery(id+"F0.wireOp",EDGE,"E22.0");Q64=makeQuery(id+"F1.opExtrude","CAP_EDGE",EDGE,{"disambiguationData":[OSD([subQ0]),TDD([makeQuery(id+"F0.imprint","IMPRINT",EDGE,{"disambiguationData":[TD([[makeQuery(id+"F0.imprint","INTERSECT",VERTEX,{"derivedFrom":[sQuery(id+"F0.wireOp",EDGE,"E10.0"),subQ0]}),-1.0]])],"derivedFrom":subQ0})])],"isStart":false});}
            var Q65;
            {var subQ0=sQuery(id+"F0.wireOp",EDGE,"E23.0");Q65=makeQuery(id+"F1.opExtrude","CAP_EDGE",EDGE,{"disambiguationData":[OSD([subQ0]),TDD([makeQuery(id+"F0.imprint","IMPRINT",EDGE,{"disambiguationData":[TD([[makeQuery(id+"F0.imprint","INTERSECT",VERTEX,{"derivedFrom":[sQuery(id+"F0.wireOp",EDGE,"E10.0"),subQ0]}),-1.0]])],"derivedFrom":subQ0})])],"isStart":false});}
            var Q66;
            {var subQ0=sQuery(id+"F0.wireOp",EDGE,"E23.0");Q66=makeQuery(id+"F1.opExtrude","CAP_EDGE",EDGE,{"disambiguationData":[OSD([subQ0]),TDD([makeQuery(id+"F0.imprint","IMPRINT",EDGE,{"disambiguationData":[TD([[makeQuery(id+"F0.imprint","INTERSECT",VERTEX,{"derivedFrom":[sQuery(id+"F0.wireOp",EDGE,"E6.0"),subQ0]}),-1.0]])],"derivedFrom":subQ0})])],"isStart":false});}
            var Q67;
            {var subQ0=sQuery(id+"F0.wireOp",EDGE,"E6.0");Q67=makeQuery(id+"F1.opExtrude","CAP_EDGE",EDGE,{"disambiguationData":[OSD([subQ0]),TDD([makeQuery(id+"F0.imprint","IMPRINT",EDGE,{"disambiguationData":[TD([[makeQuery(id+"F0.imprint","INTERSECT",VERTEX,{"derivedFrom":[subQ0,sQuery(id+"F0.wireOp",EDGE,"E23.0")]}),-1.0]])],"derivedFrom":subQ0})])],"isStart":false});}
            var Q68;
            {var subQ0=sQuery(id+"F0.wireOp",EDGE,"E6.0");Q68=makeQuery(id+"F1.opExtrude","CAP_EDGE",EDGE,{"disambiguationData":[OSD([subQ0]),TDD([makeQuery(id+"F0.imprint","IMPRINT",EDGE,{"disambiguationData":[TD([[makeQuery(id+"F0.imprint","INTERSECT",VERTEX,{"derivedFrom":[subQ0,sQuery(id+"F0.wireOp",EDGE,"E21.0")]}),-1.0]])],"derivedFrom":subQ0})])],"isStart":false});}
            fillet(context, id + "F3", {"entities" : qUnion([Q0, Q1, Q2, Q3, Q4, Q5, Q6, Q7, Q8, Q9, Q10, Q11, Q12, Q13, Q14, Q15, Q16, Q17, Q18, Q19, Q20, Q21, Q22, Q23, Q24, Q25, Q26, Q27, Q28, Q29, Q30, Q31, Q32, Q33, Q34, Q35, Q36, Q37, Q38, Q39, Q40, Q41, Q42, Q43, Q44, Q45, Q46, Q47, Q48, Q49, Q50, Q51, Q52, Q53, Q54, Q55, Q56, Q57, Q58, Q59, Q60, Q61, Q62, Q63, Q64, Q65, Q66, Q67, Q68]), "radius" : .65 * mm, "tangentPropagation" : true, "allowEdgeOverflow" : false});
        }
        {
            var Q0;
            {var subQ0=sQuery(id+"F0.wireOp",EDGE,"85c74178-88a3-4eaf-b492-32c6037f9e62.0");var subQ1=sQuery(id+"F0.wireOp",EDGE,"3e5cf576-49dc-4465-ad3e-ca1242db3cf5.0");var subQ2=makeQuery(id+"F0.imprint","INTERSECT",VERTEX,{"derivedFrom":[subQ1,subQ0]});Q0=makeQuery(id+"F0.imprint","IMPRINT",FACE,{"disambiguationData":[TD([[makeQuery(id+"F0.imprint","IMPRINT",EDGE,{"disambiguationData":[TD([[subQ2,-1.0]])],"derivedFrom":subQ1}),1.0]])]});}
            var Q1;
            {var subQ0=sQuery(id+"F0.wireOp",EDGE,"450db5bc-e2e3-4f88-b9d5-953014a2ba1e.0");var subQ1=sQuery(id+"F0.wireOp",EDGE,"3e5cf576-49dc-4465-ad3e-ca1242db3cf5.0");var subQ2=makeQuery(id+"F0.imprint","INTERSECT",VERTEX,{"derivedFrom":[subQ1,subQ0]});Q1=makeQuery(id+"F0.imprint","IMPRINT",FACE,{"disambiguationData":[TD([[makeQuery(id+"F0.imprint","IMPRINT",EDGE,{"disambiguationData":[TD([[subQ2,-1.0]])],"derivedFrom":subQ1}),1.0]])]});}
            var Q2;
            {var subQ0=sQuery(id+"F0.wireOp",EDGE,"681770c7-baf9-4a3d-b09d-7c4e2b6cc42b.0");var subQ1=sQuery(id+"F0.wireOp",EDGE,"3e5cf576-49dc-4465-ad3e-ca1242db3cf5.0");var subQ2=makeQuery(id+"F0.imprint","INTERSECT",VERTEX,{"derivedFrom":[subQ1,subQ0]});Q2=makeQuery(id+"F0.imprint","IMPRINT",FACE,{"disambiguationData":[TD([[makeQuery(id+"F0.imprint","IMPRINT",EDGE,{"disambiguationData":[TD([[subQ2,-1.0]])],"derivedFrom":subQ1}),1.0]])]});}
            var Q3;
            {var subQ0=sQuery(id+"F0.wireOp",EDGE,"0c15ec7b-9e92-4eb4-8615-29722b4b26f3.0");var subQ1=sQuery(id+"F0.wireOp",EDGE,"3e5cf576-49dc-4465-ad3e-ca1242db3cf5.0");var subQ2=makeQuery(id+"F0.imprint","INTERSECT",VERTEX,{"derivedFrom":[subQ1,subQ0]});Q3=makeQuery(id+"F0.imprint","IMPRINT",FACE,{"disambiguationData":[TD([[makeQuery(id+"F0.imprint","IMPRINT",EDGE,{"disambiguationData":[TD([[subQ2,-1.0]])],"derivedFrom":subQ1}),1.0]])]});}
            var Q4;
            {var subQ0=sQuery(id+"F0.wireOp",EDGE,"0c15ec7b-9e92-4eb4-8615-29722b4b26f3.0");var subQ1=sQuery(id+"F0.wireOp",EDGE,"9343b0c3-cd2f-487d-bd13-aee8d7f259e0.0");var subQ2=makeQuery(id+"F0.imprint","INTERSECT",VERTEX,{"derivedFrom":[subQ1,subQ0]});Q4=makeQuery(id+"F0.imprint","IMPRINT",FACE,{"disambiguationData":[TD([[makeQuery(id+"F0.imprint","IMPRINT",EDGE,{"disambiguationData":[TD([[subQ2,-1.0]])],"derivedFrom":subQ1}),1.0]])]});}
            var Q5;
            {var subQ0=sQuery(id+"F0.wireOp",EDGE,"681770c7-baf9-4a3d-b09d-7c4e2b6cc42b.0");var subQ1=sQuery(id+"F0.wireOp",EDGE,"9343b0c3-cd2f-487d-bd13-aee8d7f259e0.0");var subQ2=makeQuery(id+"F0.imprint","INTERSECT",VERTEX,{"derivedFrom":[subQ1,subQ0]});Q5=makeQuery(id+"F0.imprint","IMPRINT",FACE,{"disambiguationData":[TD([[makeQuery(id+"F0.imprint","IMPRINT",EDGE,{"disambiguationData":[TD([[subQ2,-1.0]])],"derivedFrom":subQ1}),1.0]])]});}
            var Q6;
            {var subQ0=sQuery(id+"F0.wireOp",EDGE,"450db5bc-e2e3-4f88-b9d5-953014a2ba1e.0");var subQ1=sQuery(id+"F0.wireOp",EDGE,"9343b0c3-cd2f-487d-bd13-aee8d7f259e0.0");var subQ2=makeQuery(id+"F0.imprint","INTERSECT",VERTEX,{"derivedFrom":[subQ1,subQ0]});Q6=makeQuery(id+"F0.imprint","IMPRINT",FACE,{"disambiguationData":[TD([[makeQuery(id+"F0.imprint","IMPRINT",EDGE,{"disambiguationData":[TD([[subQ2,-1.0]])],"derivedFrom":subQ1}),1.0]])]});}
            var Q7;
            {var subQ0=sQuery(id+"F0.wireOp",EDGE,"85c74178-88a3-4eaf-b492-32c6037f9e62.0");var subQ1=sQuery(id+"F0.wireOp",EDGE,"9343b0c3-cd2f-487d-bd13-aee8d7f259e0.0");var subQ2=makeQuery(id+"F0.imprint","INTERSECT",VERTEX,{"derivedFrom":[subQ1,subQ0]});Q7=makeQuery(id+"F0.imprint","IMPRINT",FACE,{"disambiguationData":[TD([[makeQuery(id+"F0.imprint","IMPRINT",EDGE,{"disambiguationData":[TD([[subQ2,-1.0]])],"derivedFrom":subQ1}),1.0]])]});}
            var Q8;
            {var subQ0=sQuery(id+"F0.wireOp",EDGE,"85c74178-88a3-4eaf-b492-32c6037f9e62.0");var subQ1=sQuery(id+"F0.wireOp",EDGE,"bdac1eed-a409-4cee-9b7b-61454a391d7d.0");var subQ2=makeQuery(id+"F0.imprint","INTERSECT",VERTEX,{"derivedFrom":[subQ1,subQ0]});Q8=makeQuery(id+"F0.imprint","IMPRINT",FACE,{"disambiguationData":[TD([[makeQuery(id+"F0.imprint","IMPRINT",EDGE,{"disambiguationData":[TD([[subQ2,-1.0]])],"derivedFrom":subQ1}),-1.0]])]});}
            var Q9;
            {var subQ0=sQuery(id+"F0.wireOp",EDGE,"450db5bc-e2e3-4f88-b9d5-953014a2ba1e.0");var subQ1=sQuery(id+"F0.wireOp",EDGE,"bdac1eed-a409-4cee-9b7b-61454a391d7d.0");var subQ2=makeQuery(id+"F0.imprint","INTERSECT",VERTEX,{"derivedFrom":[subQ1,subQ0]});Q9=makeQuery(id+"F0.imprint","IMPRINT",FACE,{"disambiguationData":[TD([[makeQuery(id+"F0.imprint","IMPRINT",EDGE,{"disambiguationData":[TD([[subQ2,-1.0]])],"derivedFrom":subQ1}),-1.0]])]});}
            var Q10;
            {var subQ0=sQuery(id+"F0.wireOp",EDGE,"681770c7-baf9-4a3d-b09d-7c4e2b6cc42b.0");var subQ1=sQuery(id+"F0.wireOp",EDGE,"bdac1eed-a409-4cee-9b7b-61454a391d7d.0");var subQ2=makeQuery(id+"F0.imprint","INTERSECT",VERTEX,{"derivedFrom":[subQ1,subQ0]});Q10=makeQuery(id+"F0.imprint","IMPRINT",FACE,{"disambiguationData":[TD([[makeQuery(id+"F0.imprint","IMPRINT",EDGE,{"disambiguationData":[TD([[subQ2,-1.0]])],"derivedFrom":subQ1}),-1.0]])]});}
            var Q11;
            {var subQ0=sQuery(id+"F0.wireOp",EDGE,"854f07df-45a9-419d-971c-554534df12f4.0");var subQ1=sQuery(id+"F0.wireOp",EDGE,"bdac1eed-a409-4cee-9b7b-61454a391d7d.0");var subQ2=makeQuery(id+"F0.imprint","INTERSECT",VERTEX,{"derivedFrom":[subQ1,subQ0]});Q11=makeQuery(id+"F0.imprint","IMPRINT",FACE,{"disambiguationData":[TD([[makeQuery(id+"F0.imprint","IMPRINT",EDGE,{"disambiguationData":[TD([[subQ2,1.0]])],"derivedFrom":subQ1}),-1.0]])]});}
            var Q12;
            {var subQ0=sQuery(id+"F0.wireOp",EDGE,"854f07df-45a9-419d-971c-554534df12f4.0");var subQ1=sQuery(id+"F0.wireOp",EDGE,"a62689d6-4df4-411d-a8de-d30e4e7abbb4.0");var subQ2=makeQuery(id+"F0.imprint","INTERSECT",VERTEX,{"derivedFrom":[subQ1,subQ0]});Q12=makeQuery(id+"F0.imprint","IMPRINT",FACE,{"disambiguationData":[TD([[makeQuery(id+"F0.imprint","IMPRINT",EDGE,{"disambiguationData":[TD([[subQ2,1.0]])],"derivedFrom":subQ1}),-1.0]])]});}
            var Q13;
            {var subQ0=sQuery(id+"F0.wireOp",EDGE,"681770c7-baf9-4a3d-b09d-7c4e2b6cc42b.0");var subQ1=sQuery(id+"F0.wireOp",EDGE,"a62689d6-4df4-411d-a8de-d30e4e7abbb4.0");var subQ2=makeQuery(id+"F0.imprint","INTERSECT",VERTEX,{"derivedFrom":[subQ1,subQ0]});Q13=makeQuery(id+"F0.imprint","IMPRINT",FACE,{"disambiguationData":[TD([[makeQuery(id+"F0.imprint","IMPRINT",EDGE,{"disambiguationData":[TD([[subQ2,-1.0]])],"derivedFrom":subQ1}),-1.0]])]});}
            var Q14;
            {var subQ0=sQuery(id+"F0.wireOp",EDGE,"450db5bc-e2e3-4f88-b9d5-953014a2ba1e.0");var subQ1=sQuery(id+"F0.wireOp",EDGE,"a62689d6-4df4-411d-a8de-d30e4e7abbb4.0");var subQ2=makeQuery(id+"F0.imprint","INTERSECT",VERTEX,{"derivedFrom":[subQ1,subQ0]});Q14=makeQuery(id+"F0.imprint","IMPRINT",FACE,{"disambiguationData":[TD([[makeQuery(id+"F0.imprint","IMPRINT",EDGE,{"disambiguationData":[TD([[subQ2,-1.0]])],"derivedFrom":subQ1}),-1.0]])]});}
            var Q15;
            {var subQ0=sQuery(id+"F0.wireOp",EDGE,"85c74178-88a3-4eaf-b492-32c6037f9e62.0");var subQ1=sQuery(id+"F0.wireOp",EDGE,"a62689d6-4df4-411d-a8de-d30e4e7abbb4.0");var subQ2=makeQuery(id+"F0.imprint","INTERSECT",VERTEX,{"derivedFrom":[subQ1,subQ0]});Q15=makeQuery(id+"F0.imprint","IMPRINT",FACE,{"disambiguationData":[TD([[makeQuery(id+"F0.imprint","IMPRINT",EDGE,{"disambiguationData":[TD([[subQ2,-1.0]])],"derivedFrom":subQ1}),-1.0]])]});}
            var Q16;
            {var subQ0=sQuery(id+"F0.wireOp",EDGE,"85c74178-88a3-4eaf-b492-32c6037f9e62.0");var subQ1=sQuery(id+"F0.wireOp",EDGE,"862523a1-1db9-4ec9-a786-b55df2c1a98e.0");var subQ2=makeQuery(id+"F0.imprint","INTERSECT",VERTEX,{"derivedFrom":[subQ1,subQ0]});Q16=makeQuery(id+"F0.imprint","IMPRINT",FACE,{"disambiguationData":[TD([[makeQuery(id+"F0.imprint","IMPRINT",EDGE,{"disambiguationData":[TD([[subQ2,-1.0]])],"derivedFrom":subQ1}),-1.0]])]});}
            var Q17;
            {var subQ0=sQuery(id+"F0.wireOp",EDGE,"450db5bc-e2e3-4f88-b9d5-953014a2ba1e.0");var subQ1=sQuery(id+"F0.wireOp",EDGE,"862523a1-1db9-4ec9-a786-b55df2c1a98e.0");var subQ2=makeQuery(id+"F0.imprint","INTERSECT",VERTEX,{"derivedFrom":[subQ1,subQ0]});Q17=makeQuery(id+"F0.imprint","IMPRINT",FACE,{"disambiguationData":[TD([[makeQuery(id+"F0.imprint","IMPRINT",EDGE,{"disambiguationData":[TD([[subQ2,-1.0]])],"derivedFrom":subQ1}),-1.0]])]});}
            var Q18;
            {var subQ0=sQuery(id+"F0.wireOp",EDGE,"681770c7-baf9-4a3d-b09d-7c4e2b6cc42b.0");var subQ1=sQuery(id+"F0.wireOp",EDGE,"862523a1-1db9-4ec9-a786-b55df2c1a98e.0");var subQ2=makeQuery(id+"F0.imprint","INTERSECT",VERTEX,{"derivedFrom":[subQ1,subQ0]});Q18=makeQuery(id+"F0.imprint","IMPRINT",FACE,{"disambiguationData":[TD([[makeQuery(id+"F0.imprint","IMPRINT",EDGE,{"disambiguationData":[TD([[subQ2,-1.0]])],"derivedFrom":subQ1}),-1.0]])]});}
            var Q19;
            {var subQ0=sQuery(id+"F0.wireOp",EDGE,"854f07df-45a9-419d-971c-554534df12f4.0");var subQ1=sQuery(id+"F0.wireOp",EDGE,"862523a1-1db9-4ec9-a786-b55df2c1a98e.0");var subQ2=makeQuery(id+"F0.imprint","INTERSECT",VERTEX,{"derivedFrom":[subQ1,subQ0]});Q19=makeQuery(id+"F0.imprint","IMPRINT",FACE,{"disambiguationData":[TD([[makeQuery(id+"F0.imprint","IMPRINT",EDGE,{"disambiguationData":[TD([[subQ2,1.0]])],"derivedFrom":subQ1}),-1.0]])]});}
            var Q20;
            {var subQ1=sQuery(id+"F0.wireOp",EDGE,"A6zvepGp-0RaV-yEtp-beRf-P6hXOdvUpvcg");Q20=makeQuery(id+"F0.imprint","IMPRINT",FACE,{"disambiguationData":[TD([[makeQuery(id+"F0.imprint","IMPRINT",EDGE,{"derivedFrom":subQ1}),-1.0]])]});}
            var Q21;
            Q21=makeQuery(id+"F0.imprint","IMPRINT",FACE,{"disambiguationData":[TD([[makeQuery(id+"F0.imprint","IMPRINT",EDGE,{"derivedFrom":sQuery(id+"F0.wireOp",EDGE,"E34.MirrorC")}),1.0]])]});
            var Q22;
            Q22=makeQuery(id+"F0.imprint","IMPRINT",FACE,{"disambiguationData":[TD([[makeQuery(id+"F0.imprint","IMPRINT",EDGE,{"derivedFrom":sQuery(id+"F0.wireOp",EDGE,"E29.MirrorC")}),1.0]])]});
            var Q23;
            Q23=makeQuery(id+"F0.imprint","IMPRINT",FACE,{"disambiguationData":[TD([[makeQuery(id+"F0.imprint","IMPRINT",EDGE,{"derivedFrom":sQuery(id+"F0.wireOp",EDGE,"E35.MirrorC")}),-1.0]])]});
            var Q24;
            Q24=makeQuery(id+"F0.imprint","IMPRINT",FACE,{"disambiguationData":[TD([[makeQuery(id+"F0.imprint","IMPRINT",EDGE,{"derivedFrom":sQuery(id+"F0.wireOp",EDGE,"E30.MirrorC")}),-1.0]])]});
            var Q25;
            Q25=makeQuery(id+"F0.imprint","IMPRINT",FACE,{"disambiguationData":[TD([[makeQuery(id+"F0.imprint","IMPRINT",EDGE,{"derivedFrom":sQuery(id+"F0.wireOp",EDGE,"E36.MirrorC")}),1.0]])]});
            var Q26;
            Q26=makeQuery(id+"F0.imprint","IMPRINT",FACE,{"disambiguationData":[TD([[makeQuery(id+"F0.imprint","IMPRINT",EDGE,{"derivedFrom":sQuery(id+"F0.wireOp",EDGE,"E37.MirrorC")}),-1.0]])]});
            var Q27;
            Q27=makeQuery(id+"F0.imprint","IMPRINT",FACE,{"disambiguationData":[TD([[makeQuery(id+"F0.imprint","IMPRINT",EDGE,{"derivedFrom":sQuery(id+"F0.wireOp",EDGE,"E31.MirrorC")}),1.0]])]});
            var Q28;
            Q28=makeQuery(id+"F0.imprint","IMPRINT",FACE,{"disambiguationData":[TD([[makeQuery(id+"F0.imprint","IMPRINT",EDGE,{"derivedFrom":sQuery(id+"F0.wireOp",EDGE,"E32.MirrorC")}),-1.0]])]});
            var Q29;
            Q29=makeQuery(id+"F0.imprint","IMPRINT",FACE,{"disambiguationData":[TD([[makeQuery(id+"F0.imprint","IMPRINT",EDGE,{"derivedFrom":sQuery(id+"F0.wireOp",EDGE,"E38.MirrorC")}),1.0]])]});
            var Q30;
            Q30=makeQuery(id+"F0.imprint","IMPRINT",FACE,{"disambiguationData":[TD([[makeQuery(id+"F0.imprint","IMPRINT",EDGE,{"derivedFrom":sQuery(id+"F0.wireOp",EDGE,"E33.MirrorC")}),1.0]])]});
            var Q31;
            Q31=makeQuery(id+"F0.imprint","IMPRINT",FACE,{"disambiguationData":[TD([[makeQuery(id+"F0.imprint","IMPRINT",EDGE,{"derivedFrom":sQuery(id+"F0.wireOp",EDGE,"E5.MirrorC")}),1.0]])]});
            var Q32;
            Q32=makeQuery(id+"F0.imprint","IMPRINT",FACE,{"disambiguationData":[TD([[makeQuery(id+"F0.imprint","IMPRINT",EDGE,{"derivedFrom":sQuery(id+"F0.wireOp",EDGE,"E28.MirrorC")}),1.0]])]});
            var Q33;
            Q33=makeQuery(id+"F0.imprint","IMPRINT",FACE,{"disambiguationData":[TD([[makeQuery(id+"F0.imprint","IMPRINT",EDGE,{"derivedFrom":sQuery(id+"F0.wireOp",EDGE,"E27.MirrorC")}),-1.0]])]});
            var Q34;
            Q34=makeQuery(id+"F0.imprint","IMPRINT",FACE,{"disambiguationData":[TD([[makeQuery(id+"F0.imprint","IMPRINT",EDGE,{"derivedFrom":sQuery(id+"F0.wireOp",EDGE,"E4.MirrorC")}),-1.0]])]});
            var Q35;
            Q35=makeQuery(id+"F0.imprint","IMPRINT",FACE,{"disambiguationData":[TD([[makeQuery(id+"F0.imprint","IMPRINT",EDGE,{"derivedFrom":sQuery(id+"F0.wireOp",EDGE,"E3.MirrorC")}),1.0]])]});
            var Q36;
            Q36=makeQuery(id+"F0.imprint","IMPRINT",FACE,{"disambiguationData":[TD([[makeQuery(id+"F0.imprint","IMPRINT",EDGE,{"derivedFrom":sQuery(id+"F0.wireOp",EDGE,"E26.MirrorC")}),1.0]])]});
            var Q37;
            Q37=makeQuery(id+"F0.imprint","IMPRINT",FACE,{"disambiguationData":[TD([[makeQuery(id+"F0.imprint","IMPRINT",EDGE,{"derivedFrom":sQuery(id+"F0.wireOp",EDGE,"E2.MirrorC")}),-1.0]])]});
            var Q38;
            Q38=makeQuery(id+"F0.imprint","IMPRINT",FACE,{"disambiguationData":[TD([[makeQuery(id+"F0.imprint","IMPRINT",EDGE,{"derivedFrom":sQuery(id+"F0.wireOp",EDGE,"E25.MirrorC")}),-1.0]])]});
            var Q39;
            Q39=makeQuery(id+"F0.imprint","IMPRINT",FACE,{"disambiguationData":[TD([[makeQuery(id+"F0.imprint","IMPRINT",EDGE,{"derivedFrom":sQuery(id+"F0.wireOp",EDGE,"E24.MirrorC")}),1.0]])]});
            var Q40;
            Q40=makeQuery(id+"F0.imprint","IMPRINT",FACE,{"disambiguationData":[TD([[makeQuery(id+"F0.imprint","IMPRINT",EDGE,{"derivedFrom":sQuery(id+"F0.wireOp",EDGE,"E1.MirrorC")}),1.0]])]});
            extrude(context, id + "F4", {"entities" : qUnion([Q0, Q1, Q2, Q3, Q4, Q5, Q6, Q7, Q8, Q9, Q10, Q11, Q12, Q13, Q14, Q15, Q16, Q17, Q18, Q19, Q20, Q21, Q22, Q23, Q24, Q25, Q26, Q27, Q28, Q29, Q30, Q31, Q32, Q33, Q34, Q35, Q36, Q37, Q38, Q39, Q40]), "operationType" : NewBodyOperationType.ADD, "depth" : 2.4 * mm, "offsetDistance" : 25 * mm});
        }
        {
            var Q0;
            Q0=makeQuery(id+"F4.opExtrude","CAP_EDGE",EDGE,{"disambiguationData":[OSD([sQuery(id+"F0.wireOp",EDGE,"E1.MirrorC")])],"isStart":true});
            var Q1;
            Q1=makeQuery(id+"F4.opExtrude","CAP_EDGE",EDGE,{"disambiguationData":[OSD([sQuery(id+"F0.wireOp",EDGE,"e45c70dd-72e9-4e53-a9fe-07f5300714a70.MirrorC")])],"isStart":true});
            var Q2;
            Q2=makeQuery(id+"F4.opExtrude","CAP_EDGE",EDGE,{"disambiguationData":[OSD([sQuery(id+"F0.wireOp",EDGE,"bf62e1cc-238d-43f6-9004-ae9914dc0f930.MirrorC")])],"isStart":true});
            var Q3;
            Q3=makeQuery(id+"F4.opExtrude","CAP_EDGE",EDGE,{"disambiguationData":[OSD([sQuery(id+"F0.wireOp",EDGE,"m5J850PR-lZob-VrAQ-YDXQ-QM9KVRa9ob3P")])],"isStart":true});
            var Q4;
            Q4=makeQuery(id+"F4.opExtrude","CAP_EDGE",EDGE,{"disambiguationData":[OSD([sQuery(id+"F0.wireOp",EDGE,"f65b5e1c-d193-47d1-be7c-03926a7653dd0.MirrorC")])],"isStart":true});
            var Q5;
            Q5=makeQuery(id+"F4.opExtrude","CAP_EDGE",EDGE,{"disambiguationData":[OSD([sQuery(id+"F0.wireOp",EDGE,"1c223c68-bebe-4d76-9414-4f843ac2da1a0.MirrorC")])],"isStart":true});
            var Q6;
            Q6=makeQuery(id+"F4.opExtrude","CAP_EDGE",EDGE,{"disambiguationData":[OSD([sQuery(id+"F0.wireOp",EDGE,"b634271f-a7e8-4b8c-9043-494e2b2da1621.MirrorC")])],"isStart":true});
            var Q7;
            Q7=makeQuery(id+"F4.opExtrude","CAP_EDGE",EDGE,{"disambiguationData":[OSD([sQuery(id+"F0.wireOp",EDGE,"E2.MirrorC")])],"isStart":true});
            var Q8;
            Q8=makeQuery(id+"F4.opExtrude","CAP_EDGE",EDGE,{"disambiguationData":[OSD([sQuery(id+"F0.wireOp",EDGE,"E3.MirrorC")])],"isStart":true});
            var Q9;
            Q9=makeQuery(id+"F4.opExtrude","CAP_EDGE",EDGE,{"disambiguationData":[OSD([sQuery(id+"F0.wireOp",EDGE,"370f92f0-ac8e-4000-a16d-7ad83fffce971.MirrorC")])],"isStart":true});
            var Q10;
            Q10=makeQuery(id+"F4.opExtrude","CAP_EDGE",EDGE,{"disambiguationData":[OSD([sQuery(id+"F0.wireOp",EDGE,"370f92f0-ac8e-4000-a16d-7ad83fffce970.MirrorC")])],"isStart":true});
            var Q11;
            Q11=makeQuery(id+"F4.opExtrude","CAP_EDGE",EDGE,{"disambiguationData":[OSD([sQuery(id+"F0.wireOp",EDGE,"370f92f0-ac8e-4000-a16d-7ad83fffce977.MirrorC")])],"isStart":true});
            var Q12;
            Q12=makeQuery(id+"F4.opExtrude","CAP_EDGE",EDGE,{"disambiguationData":[OSD([sQuery(id+"F0.wireOp",EDGE,"370f92f0-ac8e-4000-a16d-7ad83fffce976.MirrorC")])],"isStart":true});
            var Q13;
            Q13=makeQuery(id+"F4.opExtrude","CAP_EDGE",EDGE,{"disambiguationData":[OSD([sQuery(id+"F0.wireOp",EDGE,"470014f8-5400-498e-8aef-119e7555b1ad3.MirrorC")])],"isStart":true});
            var Q14;
            Q14=makeQuery(id+"F4.opExtrude","CAP_EDGE",EDGE,{"disambiguationData":[OSD([sQuery(id+"F0.wireOp",EDGE,"470014f8-5400-498e-8aef-119e7555b1ad2.MirrorC")])],"isStart":true});
            var Q15;
            Q15=makeQuery(id+"F4.opExtrude","CAP_EDGE",EDGE,{"disambiguationData":[OSD([sQuery(id+"F0.wireOp",EDGE,"370f92f0-ac8e-4000-a16d-7ad83fffce975.MirrorC")])],"isStart":true});
            var Q16;
            Q16=makeQuery(id+"F4.opExtrude","CAP_EDGE",EDGE,{"disambiguationData":[OSD([sQuery(id+"F0.wireOp",EDGE,"370f92f0-ac8e-4000-a16d-7ad83fffce974.MirrorC")])],"isStart":true});
            var Q17;
            Q17=makeQuery(id+"F4.opExtrude","CAP_EDGE",EDGE,{"disambiguationData":[OSD([sQuery(id+"F0.wireOp",EDGE,"E4.MirrorC")])],"isStart":true});
            var Q18;
            Q18=makeQuery(id+"F4.opExtrude","CAP_EDGE",EDGE,{"disambiguationData":[OSD([sQuery(id+"F0.wireOp",EDGE,"E5.MirrorC")])],"isStart":true});
            var Q19;
            Q19=makeQuery(id+"F4.opExtrude","CAP_EDGE",EDGE,{"disambiguationData":[OSD([sQuery(id+"F0.wireOp",EDGE,"470014f8-5400-498e-8aef-119e7555b1ad1.MirrorC")])],"isStart":true});
            var Q20;
            Q20=makeQuery(id+"F4.opExtrude","CAP_EDGE",EDGE,{"disambiguationData":[OSD([sQuery(id+"F0.wireOp",EDGE,"E38.MirrorC")])],"isStart":true});
            var Q21;
            Q21=makeQuery(id+"F4.opExtrude","CAP_EDGE",EDGE,{"disambiguationData":[OSD([sQuery(id+"F0.wireOp",EDGE,"E36.MirrorC")])],"isStart":true});
            var Q22;
            Q22=makeQuery(id+"F4.opExtrude","CAP_EDGE",EDGE,{"disambiguationData":[OSD([sQuery(id+"F0.wireOp",EDGE,"E35.MirrorC")])],"isStart":true});
            var Q23;
            Q23=makeQuery(id+"F4.opExtrude","CAP_EDGE",EDGE,{"disambiguationData":[OSD([sQuery(id+"F0.wireOp",EDGE,"E34.MirrorC")])],"isStart":true});
            var Q24;
            Q24=makeQuery(id+"F4.opExtrude","CAP_EDGE",EDGE,{"disambiguationData":[OSD([sQuery(id+"F0.wireOp",EDGE,"E37.MirrorC")])],"isStart":true});
            var Q25;
            Q25=makeQuery(id+"F4.opExtrude","CAP_EDGE",EDGE,{"disambiguationData":[OSD([sQuery(id+"F0.wireOp",EDGE,"E33.MirrorC")])],"isStart":true});
            var Q26;
            Q26=makeQuery(id+"F4.opExtrude","CAP_EDGE",EDGE,{"disambiguationData":[OSD([sQuery(id+"F0.wireOp",EDGE,"E32.MirrorC")])],"isStart":true});
            var Q27;
            Q27=makeQuery(id+"F4.opExtrude","CAP_EDGE",EDGE,{"disambiguationData":[OSD([sQuery(id+"F0.wireOp",EDGE,"E31.MirrorC")])],"isStart":true});
            var Q28;
            Q28=makeQuery(id+"F4.opExtrude","CAP_EDGE",EDGE,{"disambiguationData":[OSD([sQuery(id+"F0.wireOp",EDGE,"E30.MirrorC")])],"isStart":true});
            var Q29;
            Q29=makeQuery(id+"F4.opExtrude","CAP_EDGE",EDGE,{"disambiguationData":[OSD([sQuery(id+"F0.wireOp",EDGE,"E29.MirrorC")])],"isStart":true});
            var Q30;
            Q30=makeQuery(id+"F4.opExtrude","CAP_EDGE",EDGE,{"disambiguationData":[OSD([sQuery(id+"F0.wireOp",EDGE,"E26.MirrorC")])],"isStart":true});
            var Q31;
            Q31=makeQuery(id+"F4.opExtrude","CAP_EDGE",EDGE,{"disambiguationData":[OSD([sQuery(id+"F0.wireOp",EDGE,"E27.MirrorC")])],"isStart":true});
            var Q32;
            Q32=makeQuery(id+"F4.opExtrude","CAP_EDGE",EDGE,{"disambiguationData":[OSD([sQuery(id+"F0.wireOp",EDGE,"E28.MirrorC")])],"isStart":true});
            var Q33;
            Q33=makeQuery(id+"F4.opExtrude","CAP_EDGE",EDGE,{"disambiguationData":[OSD([sQuery(id+"F0.wireOp",EDGE,"E25.MirrorC")])],"isStart":true});
            var Q34;
            Q34=makeQuery(id+"F4.opExtrude","CAP_EDGE",EDGE,{"disambiguationData":[OSD([sQuery(id+"F0.wireOp",EDGE,"E24.MirrorC")])],"isStart":true});
            fillet(context, id + "F5", {"entities" : qUnion([Q0, Q1, Q2, Q3, Q4, Q5, Q6, Q7, Q8, Q9, Q10, Q11, Q12, Q13, Q14, Q15, Q16, Q17, Q18, Q19, Q20, Q21, Q22, Q23, Q24, Q25, Q26, Q27, Q28, Q29, Q30, Q31, Q32, Q33, Q34]), "radius" : 2 * mm, "tangentPropagation" : true, "allowEdgeOverflow" : false});
        }
    });
